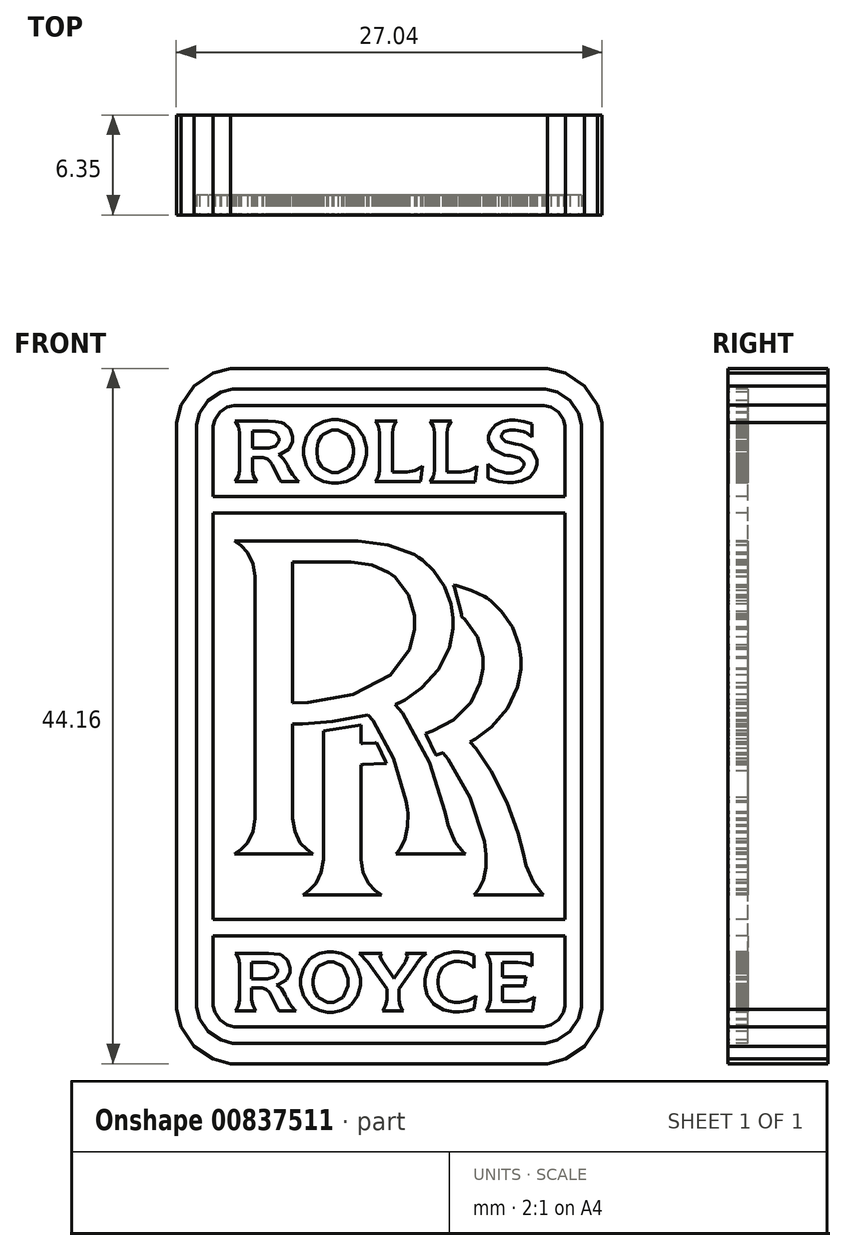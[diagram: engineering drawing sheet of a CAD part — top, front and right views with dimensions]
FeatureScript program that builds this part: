
annotation { "Feature Type Name" : "Feature", "Feature Type Description" : "" }
export const myFeature = defineFeature(function(context is Context, id is Id, definition is map)
    precondition{}
    {
        {
            var Q0;
            Q0=qCreatedBy(makeId("Front.planeOp"),FACE);
            var sketch = newSketch(context, id + "F0", { "sketchPlane" : qUnion([Q0])});
            skLineSegment(sketch, "E0", {"start": v(13.52, 18.27) * mm, "end": v(13.52, 18.64) * mm});
            skLineSegment(sketch, "E1", {"start": v(13.52, 18.64) * mm, "end": v(13.22, 19.75) * mm});
            skLineSegment(sketch, "E2", {"start": v(13.22, 19.75) * mm, "end": v(12.4, 20.97) * mm});
            skLineSegment(sketch, "E3", {"start": v(12.4, 20.97) * mm, "end": v(11.19, 21.79) * mm});
            skLineSegment(sketch, "E4", {"start": v(11.19, 21.79) * mm, "end": v(10.07, 22.08) * mm});
            skLineSegment(sketch, "E5", {"start": v(10.07, 22.08) * mm, "end": v(9.7, 22.08) * mm});
            skLineSegment(sketch, "E6", {"start": v(9.7, 22.08) * mm, "end": v(-9.7, 22.08) * mm});
            skLineSegment(sketch, "E7", {"start": v(-9.7, 22.08) * mm, "end": v(-10.07, 22.08) * mm});
            skLineSegment(sketch, "E8", {"start": v(-10.07, 22.08) * mm, "end": v(-11.19, 21.79) * mm});
            skLineSegment(sketch, "E9", {"start": v(-11.19, 21.79) * mm, "end": v(-12.4, 20.97) * mm});
            skLineSegment(sketch, "E10", {"start": v(-12.4, 20.97) * mm, "end": v(-13.22, 19.75) * mm});
            skLineSegment(sketch, "E11", {"start": v(-13.22, 19.75) * mm, "end": v(-13.52, 18.64) * mm});
            skLineSegment(sketch, "E12", {"start": v(-13.52, 18.64) * mm, "end": v(-13.52, 18.27) * mm});
            skLineSegment(sketch, "E13", {"start": v(-13.52, 18.27) * mm, "end": v(-13.52, -18.26) * mm});
            skLineSegment(sketch, "E14", {"start": v(-13.52, -18.26) * mm, "end": v(-13.52, -18.64) * mm});
            skLineSegment(sketch, "E15", {"start": v(-13.52, -18.64) * mm, "end": v(-13.22, -19.75) * mm});
            skLineSegment(sketch, "E16", {"start": v(-13.22, -19.75) * mm, "end": v(-12.4, -20.97) * mm});
            skLineSegment(sketch, "E17", {"start": v(-12.4, -20.97) * mm, "end": v(-11.19, -21.78) * mm});
            skLineSegment(sketch, "E18", {"start": v(-11.19, -21.78) * mm, "end": v(-10.07, -22.08) * mm});
            skLineSegment(sketch, "E19", {"start": v(-10.07, -22.08) * mm, "end": v(-9.7, -22.08) * mm});
            skLineSegment(sketch, "E20", {"start": v(-9.7, -22.08) * mm, "end": v(9.7, -22.08) * mm});
            skLineSegment(sketch, "E21", {"start": v(9.7, -22.08) * mm, "end": v(10.07, -22.08) * mm});
            skLineSegment(sketch, "E22", {"start": v(10.07, -22.08) * mm, "end": v(11.19, -21.78) * mm});
            skLineSegment(sketch, "E23", {"start": v(11.19, -21.78) * mm, "end": v(12.4, -20.97) * mm});
            skLineSegment(sketch, "E24", {"start": v(12.4, -20.97) * mm, "end": v(13.22, -19.75) * mm});
            skLineSegment(sketch, "E25", {"start": v(13.22, -19.75) * mm, "end": v(13.52, -18.64) * mm});
            skLineSegment(sketch, "E26", {"start": v(13.52, -18.64) * mm, "end": v(13.52, -18.26) * mm});
            skLineSegment(sketch, "E27", {"start": v(13.52, -18.26) * mm, "end": v(13.52, 18.27) * mm});
            skSolve(sketch);
        }
        {
            var Q0;
            Q0 = qSketchRegion(id + "F0", true);
            extrude(context, id + "F1", {"entities" : qUnion([Q0]), "depth" : 6.35 * mm, "offsetDistance" : 25.4 * mm});
        }
        {
            var Q0;
            Q0=makeQuery(id+"F1.opExtrude","CAP_FACE",FACE,{"disambiguationData":[OSD([sQuery(id+"F0.wireOp",EDGE,"E0"),sQuery(id+"F0.wireOp",EDGE,"E1"),sQuery(id+"F0.wireOp",EDGE,"E2"),sQuery(id+"F0.wireOp",EDGE,"E3"),sQuery(id+"F0.wireOp",EDGE,"E4"),sQuery(id+"F0.wireOp",EDGE,"E5"),sQuery(id+"F0.wireOp",EDGE,"E6"),sQuery(id+"F0.wireOp",EDGE,"E7"),sQuery(id+"F0.wireOp",EDGE,"E8"),sQuery(id+"F0.wireOp",EDGE,"E9"),sQuery(id+"F0.wireOp",EDGE,"E10"),sQuery(id+"F0.wireOp",EDGE,"E11"),sQuery(id+"F0.wireOp",EDGE,"E12"),sQuery(id+"F0.wireOp",EDGE,"E13"),sQuery(id+"F0.wireOp",EDGE,"E14"),sQuery(id+"F0.wireOp",EDGE,"E15"),sQuery(id+"F0.wireOp",EDGE,"E16"),sQuery(id+"F0.wireOp",EDGE,"E17"),sQuery(id+"F0.wireOp",EDGE,"E18"),sQuery(id+"F0.wireOp",EDGE,"E19"),sQuery(id+"F0.wireOp",EDGE,"E20"),sQuery(id+"F0.wireOp",EDGE,"E21"),sQuery(id+"F0.wireOp",EDGE,"E22"),sQuery(id+"F0.wireOp",EDGE,"E23"),sQuery(id+"F0.wireOp",EDGE,"E24"),sQuery(id+"F0.wireOp",EDGE,"E25"),sQuery(id+"F0.wireOp",EDGE,"E26"),sQuery(id+"F0.wireOp",EDGE,"E27")])],"isStart":false});
            var sketch = newSketch(context, id + "F2", { "sketchPlane" : qUnion([Q0])});
            skLineSegment(sketch, "E28", {"start": v(-12.23, 18.27) * mm, "end": v(-12.23, 18.51) * mm});
            skLineSegment(sketch, "E29", {"start": v(-12.23, 18.51) * mm, "end": v(-12.03, 19.24) * mm});
            skLineSegment(sketch, "E30", {"start": v(-12.03, 19.24) * mm, "end": v(-11.49, 20.04) * mm});
            skLineSegment(sketch, "E31", {"start": v(-11.49, 20.04) * mm, "end": v(-10.69, 20.58) * mm});
            skLineSegment(sketch, "E32", {"start": v(-10.69, 20.58) * mm, "end": v(-9.95, 20.78) * mm});
            skLineSegment(sketch, "E33", {"start": v(-9.95, 20.78) * mm, "end": v(-9.7, 20.78) * mm});
            skLineSegment(sketch, "E34", {"start": v(-9.7, 20.78) * mm, "end": v(9.69, 20.78) * mm});
            skLineSegment(sketch, "E35", {"start": v(9.69, 20.78) * mm, "end": v(9.93, 20.78) * mm});
            skLineSegment(sketch, "E36", {"start": v(9.93, 20.78) * mm, "end": v(10.68, 20.58) * mm});
            skLineSegment(sketch, "E37", {"start": v(10.68, 20.58) * mm, "end": v(11.48, 20.04) * mm});
            skLineSegment(sketch, "E38", {"start": v(11.48, 20.04) * mm, "end": v(12.03, 19.24) * mm});
            skLineSegment(sketch, "E39", {"start": v(12.03, 19.24) * mm, "end": v(12.23, 18.51) * mm});
            skLineSegment(sketch, "E40", {"start": v(12.23, 18.51) * mm, "end": v(12.23, 18.27) * mm});
            skLineSegment(sketch, "E41", {"start": v(12.23, 18.27) * mm, "end": v(12.23, -18.26) * mm});
            skLineSegment(sketch, "E42", {"start": v(12.23, -18.26) * mm, "end": v(12.23, -18.5) * mm});
            skLineSegment(sketch, "E43", {"start": v(12.23, -18.5) * mm, "end": v(12.03, -19.24) * mm});
            skLineSegment(sketch, "E44", {"start": v(12.03, -19.24) * mm, "end": v(11.48, -20.04) * mm});
            skLineSegment(sketch, "E45", {"start": v(11.48, -20.04) * mm, "end": v(10.68, -20.58) * mm});
            skLineSegment(sketch, "E46", {"start": v(10.68, -20.58) * mm, "end": v(9.93, -20.78) * mm});
            skLineSegment(sketch, "E47", {"start": v(9.93, -20.78) * mm, "end": v(9.69, -20.78) * mm});
            skLineSegment(sketch, "E48", {"start": v(9.69, -20.78) * mm, "end": v(-9.7, -20.78) * mm});
            skLineSegment(sketch, "E49", {"start": v(-9.7, -20.78) * mm, "end": v(-9.95, -20.78) * mm});
            skLineSegment(sketch, "E50", {"start": v(-9.95, -20.78) * mm, "end": v(-10.69, -20.58) * mm});
            skLineSegment(sketch, "E51", {"start": v(-10.69, -20.58) * mm, "end": v(-11.49, -20.04) * mm});
            skLineSegment(sketch, "E52", {"start": v(-11.49, -20.04) * mm, "end": v(-12.03, -19.24) * mm});
            skLineSegment(sketch, "E53", {"start": v(-12.03, -19.24) * mm, "end": v(-12.23, -18.5) * mm});
            skLineSegment(sketch, "E54", {"start": v(-12.23, -18.5) * mm, "end": v(-12.23, -18.26) * mm});
            skLineSegment(sketch, "E55", {"start": v(-12.23, -18.26) * mm, "end": v(-12.23, 18.27) * mm});
            skLineSegment(sketch, "E56", {"start": v(-11.18, 13.96) * mm, "end": v(-11.18, 18.27) * mm});
            skLineSegment(sketch, "E57", {"start": v(-11.18, 18.27) * mm, "end": v(-11.18, 18.4) * mm});
            skLineSegment(sketch, "E58", {"start": v(-11.18, 18.4) * mm, "end": v(-11.06, 18.84) * mm});
            skLineSegment(sketch, "E59", {"start": v(-11.06, 18.84) * mm, "end": v(-10.75, 19.3) * mm});
            skLineSegment(sketch, "E60", {"start": v(-10.75, 19.3) * mm, "end": v(-10.28, 19.62) * mm});
            skLineSegment(sketch, "E61", {"start": v(-10.28, 19.62) * mm, "end": v(-9.85, 19.74) * mm});
            skLineSegment(sketch, "E62", {"start": v(-9.85, 19.74) * mm, "end": v(-9.7, 19.74) * mm});
            skLineSegment(sketch, "E63", {"start": v(-9.7, 19.74) * mm, "end": v(9.69, 19.74) * mm});
            skLineSegment(sketch, "E64", {"start": v(9.69, 19.74) * mm, "end": v(9.83, 19.74) * mm});
            skLineSegment(sketch, "E65", {"start": v(9.83, 19.74) * mm, "end": v(10.27, 19.62) * mm});
            skLineSegment(sketch, "E66", {"start": v(10.27, 19.62) * mm, "end": v(10.75, 19.3) * mm});
            skLineSegment(sketch, "E67", {"start": v(10.75, 19.3) * mm, "end": v(11.06, 18.84) * mm});
            skLineSegment(sketch, "E68", {"start": v(11.06, 18.84) * mm, "end": v(11.18, 18.4) * mm});
            skLineSegment(sketch, "E69", {"start": v(11.18, 18.4) * mm, "end": v(11.18, 18.27) * mm});
            skLineSegment(sketch, "E70", {"start": v(11.18, 18.27) * mm, "end": v(11.18, 13.96) * mm});
            skLineSegment(sketch, "E71", {"start": v(11.18, 13.96) * mm, "end": v(-11.18, 13.96) * mm});
            skLineSegment(sketch, "E72", {"start": v(-11.18, 12.9) * mm, "end": v(11.18, 12.9) * mm});
            skLineSegment(sketch, "E73", {"start": v(11.18, 12.9) * mm, "end": v(11.18, -12.9) * mm});
            skLineSegment(sketch, "E74", {"start": v(11.18, -12.9) * mm, "end": v(-11.18, -12.9) * mm});
            skLineSegment(sketch, "E75", {"start": v(-11.18, -12.9) * mm, "end": v(-11.18, 12.9) * mm});
            skLineSegment(sketch, "E76", {"start": v(6.47, 16.07) * mm, "end": v(6.49, 16.03) * mm});
            skLineSegment(sketch, "E77", {"start": v(6.49, 16.03) * mm, "end": v(6.84, 15.74) * mm});
            skLineSegment(sketch, "E78", {"start": v(6.84, 15.74) * mm, "end": v(6.87, 15.73) * mm});
            skLineSegment(sketch, "E79", {"start": v(6.87, 15.73) * mm, "end": v(6.96, 15.68) * mm});
            skLineSegment(sketch, "E80", {"start": v(6.96, 15.68) * mm, "end": v(7.66, 15.47) * mm});
            skLineSegment(sketch, "E81", {"start": v(7.66, 15.47) * mm, "end": v(7.9, 15.47) * mm});
            skLineSegment(sketch, "E82", {"start": v(7.9, 15.47) * mm, "end": v(8.05, 15.47) * mm});
            skLineSegment(sketch, "E83", {"start": v(8.05, 15.47) * mm, "end": v(8.52, 15.63) * mm});
            skLineSegment(sketch, "E84", {"start": v(8.52, 15.63) * mm, "end": v(8.75, 15.94) * mm});
            skLineSegment(sketch, "E85", {"start": v(8.75, 15.94) * mm, "end": v(8.75, 16.05) * mm});
            skLineSegment(sketch, "E86", {"start": v(8.75, 16.05) * mm, "end": v(8.75, 16.15) * mm});
            skLineSegment(sketch, "E87", {"start": v(8.75, 16.15) * mm, "end": v(8.47, 16.44) * mm});
            skLineSegment(sketch, "E88", {"start": v(8.47, 16.44) * mm, "end": v(7.88, 16.58) * mm});
            skLineSegment(sketch, "E89", {"start": v(7.88, 16.58) * mm, "end": v(7.72, 16.6) * mm});
            skLineSegment(sketch, "E90", {"start": v(7.72, 16.6) * mm, "end": v(7.53, 16.63) * mm});
            skLineSegment(sketch, "E91", {"start": v(7.53, 16.63) * mm, "end": v(6.82, 16.96) * mm});
            skLineSegment(sketch, "E92", {"start": v(6.82, 16.96) * mm, "end": v(6.5, 17.52) * mm});
            skLineSegment(sketch, "E93", {"start": v(6.5, 17.52) * mm, "end": v(6.5, 17.71) * mm});
            skLineSegment(sketch, "E94", {"start": v(6.5, 17.71) * mm, "end": v(6.51, 17.82) * mm});
            skLineSegment(sketch, "E95", {"start": v(6.51, 17.82) * mm, "end": v(6.63, 18.16) * mm});
            skLineSegment(sketch, "E96", {"start": v(6.63, 18.16) * mm, "end": v(6.93, 18.52) * mm});
            skLineSegment(sketch, "E97", {"start": v(6.93, 18.52) * mm, "end": v(7.4, 18.76) * mm});
            skLineSegment(sketch, "E98", {"start": v(7.4, 18.76) * mm, "end": v(7.85, 18.84) * mm});
            skLineSegment(sketch, "E99", {"start": v(7.85, 18.84) * mm, "end": v(8, 18.84) * mm});
            skLineSegment(sketch, "E100", {"start": v(8, 18.84) * mm, "end": v(8.2, 18.84) * mm});
            skLineSegment(sketch, "E101", {"start": v(8.2, 18.84) * mm, "end": v(8.76, 18.76) * mm});
            skLineSegment(sketch, "E102", {"start": v(8.76, 18.76) * mm, "end": v(9.2, 18.62) * mm});
            skLineSegment(sketch, "E103", {"start": v(9.2, 18.62) * mm, "end": v(9.26, 18.59) * mm});
            skLineSegment(sketch, "E104", {"start": v(9.26, 18.59) * mm, "end": v(9.26, 17.75) * mm});
            skLineSegment(sketch, "E105", {"start": v(9.26, 17.75) * mm, "end": v(9.24, 17.8) * mm});
            skLineSegment(sketch, "E106", {"start": v(9.24, 17.8) * mm, "end": v(8.84, 18.07) * mm});
            skLineSegment(sketch, "E107", {"start": v(8.84, 18.07) * mm, "end": v(8.8, 18.1) * mm});
            skLineSegment(sketch, "E108", {"start": v(8.8, 18.1) * mm, "end": v(8.73, 18.12) * mm});
            skLineSegment(sketch, "E109", {"start": v(8.73, 18.12) * mm, "end": v(8.18, 18.22) * mm});
            skLineSegment(sketch, "E110", {"start": v(8.18, 18.22) * mm, "end": v(8, 18.22) * mm});
            skLineSegment(sketch, "E111", {"start": v(8, 18.22) * mm, "end": v(7.88, 18.22) * mm});
            skLineSegment(sketch, "E112", {"start": v(7.88, 18.22) * mm, "end": v(7.5, 18.11) * mm});
            skLineSegment(sketch, "E113", {"start": v(7.5, 18.11) * mm, "end": v(7.32, 17.9) * mm});
            skLineSegment(sketch, "E114", {"start": v(7.32, 17.9) * mm, "end": v(7.32, 17.84) * mm});
            skLineSegment(sketch, "E115", {"start": v(7.32, 17.84) * mm, "end": v(7.32, 17.75) * mm});
            skLineSegment(sketch, "E116", {"start": v(7.32, 17.75) * mm, "end": v(7.58, 17.48) * mm});
            skLineSegment(sketch, "E117", {"start": v(7.58, 17.48) * mm, "end": v(8.22, 17.32) * mm});
            skLineSegment(sketch, "E118", {"start": v(8.22, 17.32) * mm, "end": v(8.4, 17.28) * mm});
            skLineSegment(sketch, "E119", {"start": v(8.4, 17.28) * mm, "end": v(8.6, 17.25) * mm});
            skLineSegment(sketch, "E120", {"start": v(8.6, 17.25) * mm, "end": v(9.28, 16.91) * mm});
            skLineSegment(sketch, "E121", {"start": v(9.28, 16.91) * mm, "end": v(9.58, 16.32) * mm});
            skLineSegment(sketch, "E122", {"start": v(9.58, 16.32) * mm, "end": v(9.58, 16.15) * mm});
            skLineSegment(sketch, "E123", {"start": v(9.58, 16.15) * mm, "end": v(9.58, 16.02) * mm});
            skLineSegment(sketch, "E124", {"start": v(9.58, 16.02) * mm, "end": v(9.46, 15.63) * mm});
            skLineSegment(sketch, "E125", {"start": v(9.46, 15.63) * mm, "end": v(9.13, 15.22) * mm});
            skLineSegment(sketch, "E126", {"start": v(9.13, 15.22) * mm, "end": v(8.6, 14.96) * mm});
            skLineSegment(sketch, "E127", {"start": v(8.6, 14.96) * mm, "end": v(8.07, 14.87) * mm});
            skLineSegment(sketch, "E128", {"start": v(8.07, 14.87) * mm, "end": v(7.9, 14.87) * mm});
            skLineSegment(sketch, "E129", {"start": v(7.9, 14.87) * mm, "end": v(7.7, 14.87) * mm});
            skLineSegment(sketch, "E130", {"start": v(7.7, 14.87) * mm, "end": v(7.14, 14.94) * mm});
            skLineSegment(sketch, "E131", {"start": v(7.14, 14.94) * mm, "end": v(6.55, 15.1) * mm});
            skLineSegment(sketch, "E132", {"start": v(6.55, 15.1) * mm, "end": v(6.47, 15.15) * mm});
            skLineSegment(sketch, "E133", {"start": v(6.47, 15.15) * mm, "end": v(6.47, 16.07) * mm});
            skLineSegment(sketch, "E134", {"start": v(-6.23, 15.9) * mm, "end": v(-6.28, 15.99) * mm});
            skLineSegment(sketch, "E135", {"start": v(-6.28, 15.99) * mm, "end": v(-6.5, 16.37) * mm});
            skLineSegment(sketch, "E136", {"start": v(-6.5, 16.37) * mm, "end": v(-6.78, 16.63) * mm});
            skLineSegment(sketch, "E137", {"start": v(-6.78, 16.63) * mm, "end": v(-6.85, 16.66) * mm});
            skLineSegment(sketch, "E138", {"start": v(-6.85, 16.66) * mm, "end": v(-6.7, 16.7) * mm});
            skLineSegment(sketch, "E139", {"start": v(-6.7, 16.7) * mm, "end": v(-6.18, 17.01) * mm});
            skLineSegment(sketch, "E140", {"start": v(-6.18, 17.01) * mm, "end": v(-5.95, 17.49) * mm});
            skLineSegment(sketch, "E141", {"start": v(-5.95, 17.49) * mm, "end": v(-5.95, 17.65) * mm});
            skLineSegment(sketch, "E142", {"start": v(-5.95, 17.65) * mm, "end": v(-5.95, 17.8) * mm});
            skLineSegment(sketch, "E143", {"start": v(-5.95, 17.8) * mm, "end": v(-6.11, 18.29) * mm});
            skLineSegment(sketch, "E144", {"start": v(-6.11, 18.29) * mm, "end": v(-6.47, 18.63) * mm});
            skLineSegment(sketch, "E145", {"start": v(-6.47, 18.63) * mm, "end": v(-6.57, 18.67) * mm});
            skLineSegment(sketch, "E146", {"start": v(-6.57, 18.67) * mm, "end": v(-6.64, 18.7) * mm});
            skLineSegment(sketch, "E147", {"start": v(-6.64, 18.7) * mm, "end": v(-7.02, 18.76) * mm});
            skLineSegment(sketch, "E148", {"start": v(-7.02, 18.76) * mm, "end": v(-7.48, 18.78) * mm});
            skLineSegment(sketch, "E149", {"start": v(-7.48, 18.78) * mm, "end": v(-7.64, 18.78) * mm});
            skLineSegment(sketch, "E150", {"start": v(-7.64, 18.78) * mm, "end": v(-9.6, 18.78) * mm});
            skLineSegment(sketch, "E151", {"start": v(-9.6, 18.78) * mm, "end": v(-9.55, 18.75) * mm});
            skLineSegment(sketch, "E152", {"start": v(-9.55, 18.75) * mm, "end": v(-9.38, 18.43) * mm});
            skLineSegment(sketch, "E153", {"start": v(-9.38, 18.43) * mm, "end": v(-9.3, 18.05) * mm});
            skLineSegment(sketch, "E154", {"start": v(-9.3, 18.05) * mm, "end": v(-9.3, 17.92) * mm});
            skLineSegment(sketch, "E155", {"start": v(-9.3, 17.92) * mm, "end": v(-9.3, 15.77) * mm});
            skLineSegment(sketch, "E156", {"start": v(-9.3, 15.77) * mm, "end": v(-9.3, 15.64) * mm});
            skLineSegment(sketch, "E157", {"start": v(-9.3, 15.64) * mm, "end": v(-9.38, 15.27) * mm});
            skLineSegment(sketch, "E158", {"start": v(-9.38, 15.27) * mm, "end": v(-9.55, 14.96) * mm});
            skLineSegment(sketch, "E159", {"start": v(-9.55, 14.96) * mm, "end": v(-9.6, 14.94) * mm});
            skLineSegment(sketch, "E160", {"start": v(-9.6, 14.94) * mm, "end": v(-8.2, 14.94) * mm});
            skLineSegment(sketch, "E161", {"start": v(-8.2, 14.94) * mm, "end": v(-8.24, 14.96) * mm});
            skLineSegment(sketch, "E162", {"start": v(-8.24, 14.96) * mm, "end": v(-8.41, 15.27) * mm});
            skLineSegment(sketch, "E163", {"start": v(-8.41, 15.27) * mm, "end": v(-8.5, 15.64) * mm});
            skLineSegment(sketch, "E164", {"start": v(-8.5, 15.64) * mm, "end": v(-8.5, 15.77) * mm});
            skLineSegment(sketch, "E165", {"start": v(-8.5, 15.77) * mm, "end": v(-8.5, 16.45) * mm});
            skLineSegment(sketch, "E166", {"start": v(-8.5, 16.45) * mm, "end": v(-7.9, 16.45) * mm});
            skLineSegment(sketch, "E167", {"start": v(-7.9, 16.45) * mm, "end": v(-7.8, 16.45) * mm});
            skLineSegment(sketch, "E168", {"start": v(-7.8, 16.45) * mm, "end": v(-7.53, 16.37) * mm});
            skLineSegment(sketch, "E169", {"start": v(-7.53, 16.37) * mm, "end": v(-7.33, 16.17) * mm});
            skLineSegment(sketch, "E170", {"start": v(-7.33, 16.17) * mm, "end": v(-7.3, 16.11) * mm});
            skLineSegment(sketch, "E171", {"start": v(-7.3, 16.11) * mm, "end": v(-7.24, 16.03) * mm});
            skLineSegment(sketch, "E172", {"start": v(-7.24, 16.03) * mm, "end": v(-6.74, 15.03) * mm});
            skLineSegment(sketch, "E173", {"start": v(-6.74, 15.03) * mm, "end": v(-6.68, 14.94) * mm});
            skLineSegment(sketch, "E174", {"start": v(-6.68, 14.94) * mm, "end": v(-5.55, 14.94) * mm});
            skLineSegment(sketch, "E175", {"start": v(-5.55, 14.94) * mm, "end": v(-5.63, 15) * mm});
            skLineSegment(sketch, "E176", {"start": v(-5.63, 15) * mm, "end": v(-5.95, 15.37) * mm});
            skLineSegment(sketch, "E177", {"start": v(-5.95, 15.37) * mm, "end": v(-6.19, 15.8) * mm});
            skLineSegment(sketch, "E178", {"start": v(-6.19, 15.8) * mm, "end": v(-6.23, 15.9) * mm});
            skLineSegment(sketch, "E179", {"start": v(-6.78, 17.6) * mm, "end": v(-6.78, 17.5) * mm});
            skLineSegment(sketch, "E180", {"start": v(-6.78, 17.5) * mm, "end": v(-7, 17.2) * mm});
            skLineSegment(sketch, "E181", {"start": v(-7, 17.2) * mm, "end": v(-7.45, 17.07) * mm});
            skLineSegment(sketch, "E182", {"start": v(-7.45, 17.07) * mm, "end": v(-7.6, 17.07) * mm});
            skLineSegment(sketch, "E183", {"start": v(-7.6, 17.07) * mm, "end": v(-8.5, 17.07) * mm});
            skLineSegment(sketch, "E184", {"start": v(-8.5, 17.07) * mm, "end": v(-8.5, 18.16) * mm});
            skLineSegment(sketch, "E185", {"start": v(-8.5, 18.16) * mm, "end": v(-7.6, 18.16) * mm});
            skLineSegment(sketch, "E186", {"start": v(-7.6, 18.16) * mm, "end": v(-7.45, 18.16) * mm});
            skLineSegment(sketch, "E187", {"start": v(-7.45, 18.16) * mm, "end": v(-7, 18.03) * mm});
            skLineSegment(sketch, "E188", {"start": v(-7, 18.03) * mm, "end": v(-6.78, 17.71) * mm});
            skLineSegment(sketch, "E189", {"start": v(-6.78, 17.71) * mm, "end": v(-6.78, 17.6) * mm});
            skLineSegment(sketch, "E190", {"start": v(-4.05, 15.83) * mm, "end": v(-4.11, 15.89) * mm});
            skLineSegment(sketch, "E191", {"start": v(-4.11, 15.89) * mm, "end": v(-4.31, 16.25) * mm});
            skLineSegment(sketch, "E192", {"start": v(-4.31, 16.25) * mm, "end": v(-4.4, 16.7) * mm});
            skLineSegment(sketch, "E193", {"start": v(-4.4, 16.7) * mm, "end": v(-4.4, 16.86) * mm});
            skLineSegment(sketch, "E194", {"start": v(-4.4, 16.86) * mm, "end": v(-4.4, 17) * mm});
            skLineSegment(sketch, "E195", {"start": v(-4.4, 17) * mm, "end": v(-4.31, 17.45) * mm});
            skLineSegment(sketch, "E196", {"start": v(-4.31, 17.45) * mm, "end": v(-4.11, 17.82) * mm});
            skLineSegment(sketch, "E197", {"start": v(-4.11, 17.82) * mm, "end": v(-4.05, 17.88) * mm});
            skLineSegment(sketch, "E198", {"start": v(-4.05, 17.88) * mm, "end": v(-4, 17.93) * mm});
            skLineSegment(sketch, "E199", {"start": v(-4, 17.93) * mm, "end": v(-3.43, 18.2) * mm});
            skLineSegment(sketch, "E200", {"start": v(-3.43, 18.2) * mm, "end": v(-3.24, 18.2) * mm});
            skLineSegment(sketch, "E201", {"start": v(-3.24, 18.2) * mm, "end": v(-3.04, 18.2) * mm});
            skLineSegment(sketch, "E202", {"start": v(-3.04, 18.2) * mm, "end": v(-2.48, 17.93) * mm});
            skLineSegment(sketch, "E203", {"start": v(-2.48, 17.93) * mm, "end": v(-2.43, 17.88) * mm});
            skLineSegment(sketch, "E204", {"start": v(-2.43, 17.88) * mm, "end": v(-2.38, 17.82) * mm});
            skLineSegment(sketch, "E205", {"start": v(-2.38, 17.82) * mm, "end": v(-2.16, 17.45) * mm});
            skLineSegment(sketch, "E206", {"start": v(-2.16, 17.45) * mm, "end": v(-2.07, 17) * mm});
            skLineSegment(sketch, "E207", {"start": v(-2.07, 17) * mm, "end": v(-2.07, 16.86) * mm});
            skLineSegment(sketch, "E208", {"start": v(-2.07, 16.86) * mm, "end": v(-2.07, 16.7) * mm});
            skLineSegment(sketch, "E209", {"start": v(-2.07, 16.7) * mm, "end": v(-2.16, 16.25) * mm});
            skLineSegment(sketch, "E210", {"start": v(-2.16, 16.25) * mm, "end": v(-2.38, 15.89) * mm});
            skLineSegment(sketch, "E211", {"start": v(-2.38, 15.89) * mm, "end": v(-2.43, 15.83) * mm});
            skLineSegment(sketch, "E212", {"start": v(-2.43, 15.83) * mm, "end": v(-2.48, 15.78) * mm});
            skLineSegment(sketch, "E213", {"start": v(-2.48, 15.78) * mm, "end": v(-3.05, 15.51) * mm});
            skLineSegment(sketch, "E214", {"start": v(-3.05, 15.51) * mm, "end": v(-3.24, 15.51) * mm});
            skLineSegment(sketch, "E215", {"start": v(-3.24, 15.51) * mm, "end": v(-3.45, 15.51) * mm});
            skLineSegment(sketch, "E216", {"start": v(-3.45, 15.51) * mm, "end": v(-4, 15.78) * mm});
            skLineSegment(sketch, "E217", {"start": v(-4, 15.78) * mm, "end": v(-4.05, 15.83) * mm});
            skLineSegment(sketch, "E218", {"start": v(-3.24, 14.83) * mm, "end": v(-3.06, 14.83) * mm});
            skLineSegment(sketch, "E219", {"start": v(-3.06, 14.83) * mm, "end": v(-2.51, 14.94) * mm});
            skLineSegment(sketch, "E220", {"start": v(-2.51, 14.94) * mm, "end": v(-2, 15.2) * mm});
            skLineSegment(sketch, "E221", {"start": v(-2, 15.2) * mm, "end": v(-1.92, 15.28) * mm});
            skLineSegment(sketch, "E222", {"start": v(-1.92, 15.28) * mm, "end": v(-1.82, 15.36) * mm});
            skLineSegment(sketch, "E223", {"start": v(-1.82, 15.36) * mm, "end": v(-1.43, 15.92) * mm});
            skLineSegment(sketch, "E224", {"start": v(-1.43, 15.92) * mm, "end": v(-1.24, 16.62) * mm});
            skLineSegment(sketch, "E225", {"start": v(-1.24, 16.62) * mm, "end": v(-1.24, 16.86) * mm});
            skLineSegment(sketch, "E226", {"start": v(-1.24, 16.86) * mm, "end": v(-1.24, 17.09) * mm});
            skLineSegment(sketch, "E227", {"start": v(-1.24, 17.09) * mm, "end": v(-1.43, 17.78) * mm});
            skLineSegment(sketch, "E228", {"start": v(-1.43, 17.78) * mm, "end": v(-1.82, 18.35) * mm});
            skLineSegment(sketch, "E229", {"start": v(-1.82, 18.35) * mm, "end": v(-1.92, 18.44) * mm});
            skLineSegment(sketch, "E230", {"start": v(-1.92, 18.44) * mm, "end": v(-2, 18.5) * mm});
            skLineSegment(sketch, "E231", {"start": v(-2, 18.5) * mm, "end": v(-2.51, 18.75) * mm});
            skLineSegment(sketch, "E232", {"start": v(-2.51, 18.75) * mm, "end": v(-3.06, 18.86) * mm});
            skLineSegment(sketch, "E233", {"start": v(-3.06, 18.86) * mm, "end": v(-3.24, 18.86) * mm});
            skLineSegment(sketch, "E234", {"start": v(-3.24, 18.86) * mm, "end": v(-3.43, 18.86) * mm});
            skLineSegment(sketch, "E235", {"start": v(-3.43, 18.86) * mm, "end": v(-3.98, 18.75) * mm});
            skLineSegment(sketch, "E236", {"start": v(-3.98, 18.75) * mm, "end": v(-4.48, 18.5) * mm});
            skLineSegment(sketch, "E237", {"start": v(-4.48, 18.5) * mm, "end": v(-4.57, 18.44) * mm});
            skLineSegment(sketch, "E238", {"start": v(-4.57, 18.44) * mm, "end": v(-4.67, 18.35) * mm});
            skLineSegment(sketch, "E239", {"start": v(-4.67, 18.35) * mm, "end": v(-5.06, 17.78) * mm});
            skLineSegment(sketch, "E240", {"start": v(-5.06, 17.78) * mm, "end": v(-5.25, 17.09) * mm});
            skLineSegment(sketch, "E241", {"start": v(-5.25, 17.09) * mm, "end": v(-5.25, 16.86) * mm});
            skLineSegment(sketch, "E242", {"start": v(-5.25, 16.86) * mm, "end": v(-5.25, 16.62) * mm});
            skLineSegment(sketch, "E243", {"start": v(-5.25, 16.62) * mm, "end": v(-5.06, 15.92) * mm});
            skLineSegment(sketch, "E244", {"start": v(-5.06, 15.92) * mm, "end": v(-4.67, 15.36) * mm});
            skLineSegment(sketch, "E245", {"start": v(-4.67, 15.36) * mm, "end": v(-4.57, 15.28) * mm});
            skLineSegment(sketch, "E246", {"start": v(-4.57, 15.28) * mm, "end": v(-4.48, 15.2) * mm});
            skLineSegment(sketch, "E247", {"start": v(-4.48, 15.2) * mm, "end": v(-3.97, 14.94) * mm});
            skLineSegment(sketch, "E248", {"start": v(-3.97, 14.94) * mm, "end": v(-3.43, 14.83) * mm});
            skLineSegment(sketch, "E249", {"start": v(-3.43, 14.83) * mm, "end": v(-3.24, 14.83) * mm});
            skLineSegment(sketch, "E250", {"start": v(2.3, 15.92) * mm, "end": v(2.25, 15.85) * mm});
            skLineSegment(sketch, "E251", {"start": v(2.25, 15.85) * mm, "end": v(1.83, 15.63) * mm});
            skLineSegment(sketch, "E252", {"start": v(1.83, 15.63) * mm, "end": v(1.32, 15.56) * mm});
            skLineSegment(sketch, "E253", {"start": v(1.32, 15.56) * mm, "end": v(1.15, 15.56) * mm});
            skLineSegment(sketch, "E254", {"start": v(1.15, 15.56) * mm, "end": v(0.4, 15.56) * mm});
            skLineSegment(sketch, "E255", {"start": v(0.4, 15.56) * mm, "end": v(0.4, 17.92) * mm});
            skLineSegment(sketch, "E256", {"start": v(0.4, 17.92) * mm, "end": v(0.4, 18.05) * mm});
            skLineSegment(sketch, "E257", {"start": v(0.4, 18.05) * mm, "end": v(0.48, 18.42) * mm});
            skLineSegment(sketch, "E258", {"start": v(0.48, 18.42) * mm, "end": v(0.64, 18.75) * mm});
            skLineSegment(sketch, "E259", {"start": v(0.64, 18.75) * mm, "end": v(0.68, 18.78) * mm});
            skLineSegment(sketch, "E260", {"start": v(0.68, 18.78) * mm, "end": v(-0.7, 18.78) * mm});
            skLineSegment(sketch, "E261", {"start": v(-0.7, 18.78) * mm, "end": v(-0.66, 18.75) * mm});
            skLineSegment(sketch, "E262", {"start": v(-0.66, 18.75) * mm, "end": v(-0.48, 18.42) * mm});
            skLineSegment(sketch, "E263", {"start": v(-0.48, 18.42) * mm, "end": v(-0.4, 18.05) * mm});
            skLineSegment(sketch, "E264", {"start": v(-0.4, 18.05) * mm, "end": v(-0.4, 17.92) * mm});
            skLineSegment(sketch, "E265", {"start": v(-0.4, 17.92) * mm, "end": v(-0.4, 15.77) * mm});
            skLineSegment(sketch, "E266", {"start": v(-0.4, 15.77) * mm, "end": v(-0.4, 15.64) * mm});
            skLineSegment(sketch, "E267", {"start": v(-0.4, 15.64) * mm, "end": v(-0.48, 15.27) * mm});
            skLineSegment(sketch, "E268", {"start": v(-0.48, 15.27) * mm, "end": v(-0.66, 14.97) * mm});
            skLineSegment(sketch, "E269", {"start": v(-0.66, 14.97) * mm, "end": v(-0.7, 14.94) * mm});
            skLineSegment(sketch, "E270", {"start": v(-0.7, 14.94) * mm, "end": v(2.18, 14.94) * mm});
            skLineSegment(sketch, "E271", {"start": v(2.18, 14.94) * mm, "end": v(2.3, 15.92) * mm});
            skLineSegment(sketch, "E272", {"start": v(5.78, 15.92) * mm, "end": v(5.73, 15.85) * mm});
            skLineSegment(sketch, "E273", {"start": v(5.73, 15.85) * mm, "end": v(5.31, 15.63) * mm});
            skLineSegment(sketch, "E274", {"start": v(5.31, 15.63) * mm, "end": v(4.75, 15.55) * mm});
            skLineSegment(sketch, "E275", {"start": v(4.75, 15.55) * mm, "end": v(4.63, 15.56) * mm});
            skLineSegment(sketch, "E276", {"start": v(4.63, 15.56) * mm, "end": v(3.86, 15.56) * mm});
            skLineSegment(sketch, "E277", {"start": v(3.86, 15.56) * mm, "end": v(3.86, 17.92) * mm});
            skLineSegment(sketch, "E278", {"start": v(3.86, 17.92) * mm, "end": v(3.86, 18.05) * mm});
            skLineSegment(sketch, "E279", {"start": v(3.86, 18.05) * mm, "end": v(3.94, 18.42) * mm});
            skLineSegment(sketch, "E280", {"start": v(3.94, 18.42) * mm, "end": v(4.11, 18.75) * mm});
            skLineSegment(sketch, "E281", {"start": v(4.11, 18.75) * mm, "end": v(4.16, 18.78) * mm});
            skLineSegment(sketch, "E282", {"start": v(4.16, 18.78) * mm, "end": v(2.77, 18.78) * mm});
            skLineSegment(sketch, "E283", {"start": v(2.77, 18.78) * mm, "end": v(2.82, 18.75) * mm});
            skLineSegment(sketch, "E284", {"start": v(2.82, 18.75) * mm, "end": v(3, 18.42) * mm});
            skLineSegment(sketch, "E285", {"start": v(3, 18.42) * mm, "end": v(3.07, 18.05) * mm});
            skLineSegment(sketch, "E286", {"start": v(3.07, 18.05) * mm, "end": v(3.07, 17.92) * mm});
            skLineSegment(sketch, "E287", {"start": v(3.07, 17.92) * mm, "end": v(3.07, 15.77) * mm});
            skLineSegment(sketch, "E288", {"start": v(3.07, 15.77) * mm, "end": v(3.07, 15.64) * mm});
            skLineSegment(sketch, "E289", {"start": v(3.07, 15.64) * mm, "end": v(3, 15.26) * mm});
            skLineSegment(sketch, "E290", {"start": v(3, 15.26) * mm, "end": v(2.82, 14.95) * mm});
            skLineSegment(sketch, "E291", {"start": v(2.82, 14.95) * mm, "end": v(2.77, 14.91) * mm});
            skLineSegment(sketch, "E292", {"start": v(2.77, 14.91) * mm, "end": v(5.63, 14.91) * mm});
            skLineSegment(sketch, "E293", {"start": v(5.63, 14.91) * mm, "end": v(5.78, 15.92) * mm});
            skLineSegment(sketch, "E294", {"start": v(-11.18, -13.96) * mm, "end": v(-11.18, -18.26) * mm});
            skLineSegment(sketch, "E295", {"start": v(-11.18, -18.26) * mm, "end": v(-11.18, -18.4) * mm});
            skLineSegment(sketch, "E296", {"start": v(-11.18, -18.4) * mm, "end": v(-11.06, -18.84) * mm});
            skLineSegment(sketch, "E297", {"start": v(-11.06, -18.84) * mm, "end": v(-10.75, -19.3) * mm});
            skLineSegment(sketch, "E298", {"start": v(-10.75, -19.3) * mm, "end": v(-10.28, -19.62) * mm});
            skLineSegment(sketch, "E299", {"start": v(-10.28, -19.62) * mm, "end": v(-9.85, -19.74) * mm});
            skLineSegment(sketch, "E300", {"start": v(-9.85, -19.74) * mm, "end": v(-9.7, -19.74) * mm});
            skLineSegment(sketch, "E301", {"start": v(-9.7, -19.74) * mm, "end": v(9.69, -19.74) * mm});
            skLineSegment(sketch, "E302", {"start": v(9.69, -19.74) * mm, "end": v(9.83, -19.74) * mm});
            skLineSegment(sketch, "E303", {"start": v(9.83, -19.74) * mm, "end": v(10.27, -19.62) * mm});
            skLineSegment(sketch, "E304", {"start": v(10.27, -19.62) * mm, "end": v(10.75, -19.3) * mm});
            skLineSegment(sketch, "E305", {"start": v(10.75, -19.3) * mm, "end": v(11.06, -18.84) * mm});
            skLineSegment(sketch, "E306", {"start": v(11.06, -18.84) * mm, "end": v(11.18, -18.4) * mm});
            skLineSegment(sketch, "E307", {"start": v(11.18, -18.4) * mm, "end": v(11.18, -18.26) * mm});
            skLineSegment(sketch, "E308", {"start": v(11.18, -18.26) * mm, "end": v(11.18, -13.96) * mm});
            skLineSegment(sketch, "E309", {"start": v(11.18, -13.96) * mm, "end": v(-11.18, -13.96) * mm});
            skLineSegment(sketch, "E310", {"start": v(-1.6, -8.8) * mm, "end": v(-1.6, -3.05) * mm});
            skLineSegment(sketch, "E311", {"start": v(-1.6, -3.05) * mm, "end": v(-1.46, -3.05) * mm});
            skLineSegment(sketch, "E312", {"start": v(-1.46, -3.05) * mm, "end": v(-0.11, -2.98) * mm});
            skLineSegment(sketch, "E313", {"start": v(-0.11, -2.98) * mm, "end": v(0.02, -2.96) * mm});
            skLineSegment(sketch, "E314", {"start": v(0.02, -2.96) * mm, "end": v(-0.03, -2.85) * mm});
            skLineSegment(sketch, "E315", {"start": v(-0.03, -2.85) * mm, "end": v(-0.54, -1.75) * mm});
            skLineSegment(sketch, "E316", {"start": v(-0.54, -1.75) * mm, "end": v(-0.6, -1.64) * mm});
            skLineSegment(sketch, "E317", {"start": v(-0.6, -1.64) * mm, "end": v(-0.68, -1.65) * mm});
            skLineSegment(sketch, "E318", {"start": v(-0.68, -1.65) * mm, "end": v(-1.52, -1.7) * mm});
            skLineSegment(sketch, "E319", {"start": v(-1.52, -1.7) * mm, "end": v(-1.6, -1.7) * mm});
            skLineSegment(sketch, "E320", {"start": v(-1.6, -1.7) * mm, "end": v(-1.6, -0.51) * mm});
            skLineSegment(sketch, "E321", {"start": v(-1.6, -0.51) * mm, "end": v(-1.79, -0.56) * mm});
            skLineSegment(sketch, "E322", {"start": v(-1.79, -0.56) * mm, "end": v(-3.78, -0.87) * mm});
            skLineSegment(sketch, "E323", {"start": v(-3.78, -0.87) * mm, "end": v(-3.99, -0.9) * mm});
            skLineSegment(sketch, "E324", {"start": v(-3.99, -0.9) * mm, "end": v(-3.99, -8.8) * mm});
            skLineSegment(sketch, "E325", {"start": v(-3.99, -8.8) * mm, "end": v(-3.99, -9.06) * mm});
            skLineSegment(sketch, "E326", {"start": v(-3.99, -9.06) * mm, "end": v(-4.12, -9.88) * mm});
            skLineSegment(sketch, "E327", {"start": v(-4.12, -9.88) * mm, "end": v(-4.46, -10.6) * mm});
            skLineSegment(sketch, "E328", {"start": v(-4.46, -10.6) * mm, "end": v(-4.88, -11.04) * mm});
            skLineSegment(sketch, "E329", {"start": v(-4.88, -11.04) * mm, "end": v(-5.19, -11.26) * mm});
            skLineSegment(sketch, "E330", {"start": v(-5.19, -11.26) * mm, "end": v(-5.3, -11.33) * mm});
            skLineSegment(sketch, "E331", {"start": v(-5.3, -11.33) * mm, "end": v(-0.3, -11.33) * mm});
            skLineSegment(sketch, "E332", {"start": v(-0.3, -11.33) * mm, "end": v(-0.4, -11.26) * mm});
            skLineSegment(sketch, "E333", {"start": v(-0.4, -11.26) * mm, "end": v(-0.7, -11.04) * mm});
            skLineSegment(sketch, "E334", {"start": v(-0.7, -11.04) * mm, "end": v(-1.13, -10.6) * mm});
            skLineSegment(sketch, "E335", {"start": v(-1.13, -10.6) * mm, "end": v(-1.46, -9.88) * mm});
            skLineSegment(sketch, "E336", {"start": v(-1.46, -9.88) * mm, "end": v(-1.6, -9.06) * mm});
            skLineSegment(sketch, "E337", {"start": v(-1.6, -9.06) * mm, "end": v(-1.6, -8.8) * mm});
            skLineSegment(sketch, "E338", {"start": v(10, -11.3) * mm, "end": v(9.9, -11.21) * mm});
            skLineSegment(sketch, "E339", {"start": v(9.9, -11.21) * mm, "end": v(9.36, -10.53) * mm});
            skLineSegment(sketch, "E340", {"start": v(9.36, -10.53) * mm, "end": v(8.9, -9.45) * mm});
            skLineSegment(sketch, "E341", {"start": v(8.9, -9.45) * mm, "end": v(8.83, -9.15) * mm});
            skLineSegment(sketch, "E342", {"start": v(8.83, -9.15) * mm, "end": v(8.74, -8.7) * mm});
            skLineSegment(sketch, "E343", {"start": v(8.74, -8.7) * mm, "end": v(8.38, -7.39) * mm});
            skLineSegment(sketch, "E344", {"start": v(8.38, -7.39) * mm, "end": v(7.67, -5.43) * mm});
            skLineSegment(sketch, "E345", {"start": v(7.67, -5.43) * mm, "end": v(6.67, -3.45) * mm});
            skLineSegment(sketch, "E346", {"start": v(6.67, -3.45) * mm, "end": v(5.7, -2.02) * mm});
            skLineSegment(sketch, "E347", {"start": v(5.7, -2.02) * mm, "end": v(5.31, -1.6) * mm});
            skLineSegment(sketch, "E348", {"start": v(5.31, -1.6) * mm, "end": v(5.68, -1.4) * mm});
            skLineSegment(sketch, "E349", {"start": v(5.68, -1.4) * mm, "end": v(6.68, -0.65) * mm});
            skLineSegment(sketch, "E350", {"start": v(6.68, -0.65) * mm, "end": v(7.7, 0.52) * mm});
            skLineSegment(sketch, "E351", {"start": v(7.7, 0.52) * mm, "end": v(8.35, 1.88) * mm});
            skLineSegment(sketch, "E352", {"start": v(8.35, 1.88) * mm, "end": v(8.58, 3.03) * mm});
            skLineSegment(sketch, "E353", {"start": v(8.58, 3.03) * mm, "end": v(8.58, 3.41) * mm});
            skLineSegment(sketch, "E354", {"start": v(8.58, 3.41) * mm, "end": v(8.58, 3.7) * mm});
            skLineSegment(sketch, "E355", {"start": v(8.58, 3.7) * mm, "end": v(8.44, 4.57) * mm});
            skLineSegment(sketch, "E356", {"start": v(8.44, 4.57) * mm, "end": v(8.03, 5.69) * mm});
            skLineSegment(sketch, "E357", {"start": v(8.03, 5.69) * mm, "end": v(7.34, 6.7) * mm});
            skLineSegment(sketch, "E358", {"start": v(7.34, 6.7) * mm, "end": v(6.66, 7.36) * mm});
            skLineSegment(sketch, "E359", {"start": v(6.66, 7.36) * mm, "end": v(6.4, 7.53) * mm});
            skLineSegment(sketch, "E360", {"start": v(6.4, 7.53) * mm, "end": v(6.25, 7.63) * mm});
            skLineSegment(sketch, "E361", {"start": v(6.25, 7.63) * mm, "end": v(5.42, 8.03) * mm});
            skLineSegment(sketch, "E362", {"start": v(5.42, 8.03) * mm, "end": v(4.48, 8.32) * mm});
            skLineSegment(sketch, "E363", {"start": v(4.48, 8.32) * mm, "end": v(4.27, 8.36) * mm});
            skLineSegment(sketch, "E364", {"start": v(4.27, 8.36) * mm, "end": v(4.34, 8.2) * mm});
            skLineSegment(sketch, "E365", {"start": v(4.34, 8.2) * mm, "end": v(4.8, 6.53) * mm});
            skLineSegment(sketch, "E366", {"start": v(4.8, 6.53) * mm, "end": v(4.8, 6.36) * mm});
            skLineSegment(sketch, "E367", {"start": v(4.8, 6.36) * mm, "end": v(5.02, 6.19) * mm});
            skLineSegment(sketch, "E368", {"start": v(5.02, 6.19) * mm, "end": v(5.8, 5.08) * mm});
            skLineSegment(sketch, "E369", {"start": v(5.8, 5.08) * mm, "end": v(6.15, 3.8) * mm});
            skLineSegment(sketch, "E370", {"start": v(6.15, 3.8) * mm, "end": v(6.15, 3.37) * mm});
            skLineSegment(sketch, "E371", {"start": v(6.15, 3.37) * mm, "end": v(6.15, 3.06) * mm});
            skLineSegment(sketch, "E372", {"start": v(6.15, 3.06) * mm, "end": v(5.97, 2.14) * mm});
            skLineSegment(sketch, "E373", {"start": v(5.97, 2.14) * mm, "end": v(5.38, 0.91) * mm});
            skLineSegment(sketch, "E374", {"start": v(5.38, 0.91) * mm, "end": v(4.26, -0.2) * mm});
            skLineSegment(sketch, "E375", {"start": v(4.26, -0.2) * mm, "end": v(2.96, -0.9) * mm});
            skLineSegment(sketch, "E376", {"start": v(2.96, -0.9) * mm, "end": v(2.5, -1.07) * mm});
            skLineSegment(sketch, "E377", {"start": v(2.5, -1.07) * mm, "end": v(2.55, -1.18) * mm});
            skLineSegment(sketch, "E378", {"start": v(2.55, -1.18) * mm, "end": v(3.11, -2.32) * mm});
            skLineSegment(sketch, "E379", {"start": v(3.11, -2.32) * mm, "end": v(3.16, -2.43) * mm});
            skLineSegment(sketch, "E380", {"start": v(3.16, -2.43) * mm, "end": v(3.2, -2.42) * mm});
            skLineSegment(sketch, "E381", {"start": v(3.2, -2.42) * mm, "end": v(3.57, -2.32) * mm});
            skLineSegment(sketch, "E382", {"start": v(3.57, -2.32) * mm, "end": v(3.6, -2.3) * mm});
            skLineSegment(sketch, "E383", {"start": v(3.6, -2.3) * mm, "end": v(3.94, -2.69) * mm});
            skLineSegment(sketch, "E384", {"start": v(3.94, -2.69) * mm, "end": v(5.34, -5.13) * mm});
            skLineSegment(sketch, "E385", {"start": v(5.34, -5.13) * mm, "end": v(6.24, -7.93) * mm});
            skLineSegment(sketch, "E386", {"start": v(6.24, -7.93) * mm, "end": v(6.32, -8.5) * mm});
            skLineSegment(sketch, "E387", {"start": v(6.32, -8.5) * mm, "end": v(6.35, -8.75) * mm});
            skLineSegment(sketch, "E388", {"start": v(6.35, -8.75) * mm, "end": v(6.35, -9.56) * mm});
            skLineSegment(sketch, "E389", {"start": v(6.35, -9.56) * mm, "end": v(6.19, -10.36) * mm});
            skLineSegment(sketch, "E390", {"start": v(6.19, -10.36) * mm, "end": v(5.9, -10.93) * mm});
            skLineSegment(sketch, "E391", {"start": v(5.9, -10.93) * mm, "end": v(5.68, -11.22) * mm});
            skLineSegment(sketch, "E392", {"start": v(5.68, -11.22) * mm, "end": v(5.6, -11.3) * mm});
            skLineSegment(sketch, "E393", {"start": v(5.6, -11.3) * mm, "end": v(10, -11.3) * mm});
            skLineSegment(sketch, "E394", {"start": v(5.04, -8.73) * mm, "end": v(4.93, -8.63) * mm});
            skLineSegment(sketch, "E395", {"start": v(4.93, -8.63) * mm, "end": v(4.38, -7.94) * mm});
            skLineSegment(sketch, "E396", {"start": v(4.38, -7.94) * mm, "end": v(3.92, -6.86) * mm});
            skLineSegment(sketch, "E397", {"start": v(3.92, -6.86) * mm, "end": v(3.86, -6.57) * mm});
            skLineSegment(sketch, "E398", {"start": v(3.86, -6.57) * mm, "end": v(3.74, -6.03) * mm});
            skLineSegment(sketch, "E399", {"start": v(3.74, -6.03) * mm, "end": v(2.75, -2.9) * mm});
            skLineSegment(sketch, "E400", {"start": v(2.75, -2.9) * mm, "end": v(1.05, 0.23) * mm});
            skLineSegment(sketch, "E401", {"start": v(1.05, 0.23) * mm, "end": v(0.58, 0.77) * mm});
            skLineSegment(sketch, "E402", {"start": v(0.58, 0.77) * mm, "end": v(0.6, 0.78) * mm});
            skLineSegment(sketch, "E403", {"start": v(0.6, 0.78) * mm, "end": v(0.79, 0.87) * mm});
            skLineSegment(sketch, "E404", {"start": v(0.79, 0.87) * mm, "end": v(0.81, 0.87) * mm});
            skLineSegment(sketch, "E405", {"start": v(0.81, 0.87) * mm, "end": v(1.2, 1.07) * mm});
            skLineSegment(sketch, "E406", {"start": v(1.2, 1.07) * mm, "end": v(2.25, 1.82) * mm});
            skLineSegment(sketch, "E407", {"start": v(2.25, 1.82) * mm, "end": v(3.33, 3.01) * mm});
            skLineSegment(sketch, "E408", {"start": v(3.33, 3.01) * mm, "end": v(4, 4.41) * mm});
            skLineSegment(sketch, "E409", {"start": v(4, 4.41) * mm, "end": v(4.25, 5.6) * mm});
            skLineSegment(sketch, "E410", {"start": v(4.25, 5.6) * mm, "end": v(4.25, 6) * mm});
            skLineSegment(sketch, "E411", {"start": v(4.25, 6) * mm, "end": v(4.25, 6.29) * mm});
            skLineSegment(sketch, "E412", {"start": v(4.25, 6.29) * mm, "end": v(4.11, 7.16) * mm});
            skLineSegment(sketch, "E413", {"start": v(4.11, 7.16) * mm, "end": v(3.7, 8.28) * mm});
            skLineSegment(sketch, "E414", {"start": v(3.7, 8.28) * mm, "end": v(3, 9.29) * mm});
            skLineSegment(sketch, "E415", {"start": v(3, 9.29) * mm, "end": v(2.33, 9.94) * mm});
            skLineSegment(sketch, "E416", {"start": v(2.33, 9.94) * mm, "end": v(2.07, 10.11) * mm});
            skLineSegment(sketch, "E417", {"start": v(2.07, 10.11) * mm, "end": v(1.8, 10.3) * mm});
            skLineSegment(sketch, "E418", {"start": v(1.8, 10.3) * mm, "end": v(0.11, 10.92) * mm});
            skLineSegment(sketch, "E419", {"start": v(0.11, 10.92) * mm, "end": v(-1.8, 11.16) * mm});
            skLineSegment(sketch, "E420", {"start": v(-1.8, 11.16) * mm, "end": v(-2.43, 11.16) * mm});
            skLineSegment(sketch, "E421", {"start": v(-2.43, 11.16) * mm, "end": v(-9.62, 11.16) * mm});
            skLineSegment(sketch, "E422", {"start": v(-9.62, 11.16) * mm, "end": v(-9.52, 11.1) * mm});
            skLineSegment(sketch, "E423", {"start": v(-9.52, 11.1) * mm, "end": v(-9.21, 10.87) * mm});
            skLineSegment(sketch, "E424", {"start": v(-9.21, 10.87) * mm, "end": v(-8.79, 10.43) * mm});
            skLineSegment(sketch, "E425", {"start": v(-8.79, 10.43) * mm, "end": v(-8.46, 9.71) * mm});
            skLineSegment(sketch, "E426", {"start": v(-8.46, 9.71) * mm, "end": v(-8.32, 8.9) * mm});
            skLineSegment(sketch, "E427", {"start": v(-8.32, 8.9) * mm, "end": v(-8.32, 8.62) * mm});
            skLineSegment(sketch, "E428", {"start": v(-8.32, 8.62) * mm, "end": v(-8.32, -6.19) * mm});
            skLineSegment(sketch, "E429", {"start": v(-8.32, -6.19) * mm, "end": v(-8.32, -6.46) * mm});
            skLineSegment(sketch, "E430", {"start": v(-8.32, -6.46) * mm, "end": v(-8.46, -7.29) * mm});
            skLineSegment(sketch, "E431", {"start": v(-8.46, -7.29) * mm, "end": v(-8.79, -8) * mm});
            skLineSegment(sketch, "E432", {"start": v(-8.79, -8) * mm, "end": v(-9.21, -8.44) * mm});
            skLineSegment(sketch, "E433", {"start": v(-9.21, -8.44) * mm, "end": v(-9.52, -8.66) * mm});
            skLineSegment(sketch, "E434", {"start": v(-9.52, -8.66) * mm, "end": v(-9.62, -8.73) * mm});
            skLineSegment(sketch, "E435", {"start": v(-9.62, -8.73) * mm, "end": v(-4.63, -8.73) * mm});
            skLineSegment(sketch, "E436", {"start": v(-4.63, -8.73) * mm, "end": v(-4.73, -8.66) * mm});
            skLineSegment(sketch, "E437", {"start": v(-4.73, -8.66) * mm, "end": v(-5.03, -8.44) * mm});
            skLineSegment(sketch, "E438", {"start": v(-5.03, -8.44) * mm, "end": v(-5.46, -8) * mm});
            skLineSegment(sketch, "E439", {"start": v(-5.46, -8) * mm, "end": v(-5.8, -7.29) * mm});
            skLineSegment(sketch, "E440", {"start": v(-5.8, -7.29) * mm, "end": v(-5.93, -6.46) * mm});
            skLineSegment(sketch, "E441", {"start": v(-5.93, -6.46) * mm, "end": v(-5.93, -6.19) * mm});
            skLineSegment(sketch, "E442", {"start": v(-5.93, -6.19) * mm, "end": v(-5.93, -0.45) * mm});
            skLineSegment(sketch, "E443", {"start": v(-5.93, -0.45) * mm, "end": v(-5.3, -0.45) * mm});
            skLineSegment(sketch, "E444", {"start": v(-5.3, -0.45) * mm, "end": v(-3.4, -0.3) * mm});
            skLineSegment(sketch, "E445", {"start": v(-3.4, -0.3) * mm, "end": v(-1.5, 0.04) * mm});
            skLineSegment(sketch, "E446", {"start": v(-1.5, 0.04) * mm, "end": v(-1.15, 0.13) * mm});
            skLineSegment(sketch, "E447", {"start": v(-1.15, 0.13) * mm, "end": v(-0.84, -0.25) * mm});
            skLineSegment(sketch, "E448", {"start": v(-0.84, -0.25) * mm, "end": v(0.46, -2.64) * mm});
            skLineSegment(sketch, "E449", {"start": v(0.46, -2.64) * mm, "end": v(1.27, -5.35) * mm});
            skLineSegment(sketch, "E450", {"start": v(1.27, -5.35) * mm, "end": v(1.34, -5.89) * mm});
            skLineSegment(sketch, "E451", {"start": v(1.34, -5.89) * mm, "end": v(1.38, -6.15) * mm});
            skLineSegment(sketch, "E452", {"start": v(1.38, -6.15) * mm, "end": v(1.37, -6.96) * mm});
            skLineSegment(sketch, "E453", {"start": v(1.37, -6.96) * mm, "end": v(1.2, -7.77) * mm});
            skLineSegment(sketch, "E454", {"start": v(1.2, -7.77) * mm, "end": v(0.92, -8.35) * mm});
            skLineSegment(sketch, "E455", {"start": v(0.92, -8.35) * mm, "end": v(0.7, -8.64) * mm});
            skLineSegment(sketch, "E456", {"start": v(0.7, -8.64) * mm, "end": v(0.62, -8.73) * mm});
            skLineSegment(sketch, "E457", {"start": v(0.62, -8.73) * mm, "end": v(5.04, -8.73) * mm});
            skLineSegment(sketch, "E458", {"start": v(-5.93, 0.87) * mm, "end": v(-5.93, 9.84) * mm});
            skLineSegment(sketch, "E459", {"start": v(-5.93, 9.84) * mm, "end": v(-2.54, 9.84) * mm});
            skLineSegment(sketch, "E460", {"start": v(-2.54, 9.84) * mm, "end": v(-2.23, 9.83) * mm});
            skLineSegment(sketch, "E461", {"start": v(-2.23, 9.83) * mm, "end": v(-0.9, 9.63) * mm});
            skLineSegment(sketch, "E462", {"start": v(-0.9, 9.63) * mm, "end": v(0.16, 9.17) * mm});
            skLineSegment(sketch, "E463", {"start": v(0.16, 9.17) * mm, "end": v(0.34, 9.05) * mm});
            skLineSegment(sketch, "E464", {"start": v(0.34, 9.05) * mm, "end": v(0.58, 8.88) * mm});
            skLineSegment(sketch, "E465", {"start": v(0.58, 8.88) * mm, "end": v(1.44, 7.74) * mm});
            skLineSegment(sketch, "E466", {"start": v(1.44, 7.74) * mm, "end": v(1.81, 6.42) * mm});
            skLineSegment(sketch, "E467", {"start": v(1.81, 6.42) * mm, "end": v(1.81, 5.98) * mm});
            skLineSegment(sketch, "E468", {"start": v(1.81, 5.98) * mm, "end": v(1.81, 5.55) * mm});
            skLineSegment(sketch, "E469", {"start": v(1.81, 5.55) * mm, "end": v(1.48, 4.27) * mm});
            skLineSegment(sketch, "E470", {"start": v(1.48, 4.27) * mm, "end": v(0.28, 2.64) * mm});
            skLineSegment(sketch, "E471", {"start": v(0.28, 2.64) * mm, "end": v(-2.1, 1.4) * mm});
            skLineSegment(sketch, "E472", {"start": v(-2.1, 1.4) * mm, "end": v(-4.97, 0.9) * mm});
            skLineSegment(sketch, "E473", {"start": v(-4.97, 0.9) * mm, "end": v(-5.93, 0.87) * mm});
            skLineSegment(sketch, "E474", {"start": v(-1.6, 2.16) * mm, "end": v(-1.6, 7.21) * mm});
            skLineSegment(sketch, "E475", {"start": v(-1.6, 7.21) * mm, "end": v(1.09, 7.21) * mm});
            skLineSegment(sketch, "E476", {"start": v(1.09, 7.21) * mm, "end": v(1.04, 7.35) * mm});
            skLineSegment(sketch, "E477", {"start": v(1.04, 7.35) * mm, "end": v(0.69, 7.96) * mm});
            skLineSegment(sketch, "E478", {"start": v(0.69, 7.96) * mm, "end": v(0.2, 8.47) * mm});
            skLineSegment(sketch, "E479", {"start": v(0.2, 8.47) * mm, "end": v(0.09, 8.56) * mm});
            skLineSegment(sketch, "E480", {"start": v(0.09, 8.56) * mm, "end": v(-5.3, 8.56) * mm});
            skLineSegment(sketch, "E481", {"start": v(-5.3, 8.56) * mm, "end": v(-5.19, 8.49) * mm});
            skLineSegment(sketch, "E482", {"start": v(-5.19, 8.49) * mm, "end": v(-4.88, 8.28) * mm});
            skLineSegment(sketch, "E483", {"start": v(-4.88, 8.28) * mm, "end": v(-4.46, 7.83) * mm});
            skLineSegment(sketch, "E484", {"start": v(-4.46, 7.83) * mm, "end": v(-4.12, 7.12) * mm});
            skLineSegment(sketch, "E485", {"start": v(-4.12, 7.12) * mm, "end": v(-3.99, 6.3) * mm});
            skLineSegment(sketch, "E486", {"start": v(-3.99, 6.3) * mm, "end": v(-3.99, 6.02) * mm});
            skLineSegment(sketch, "E487", {"start": v(-3.99, 6.02) * mm, "end": v(-3.99, 1.56) * mm});
            skLineSegment(sketch, "E488", {"start": v(-3.99, 1.56) * mm, "end": v(-3.77, 1.6) * mm});
            skLineSegment(sketch, "E489", {"start": v(-3.77, 1.6) * mm, "end": v(-1.77, 2.09) * mm});
            skLineSegment(sketch, "E490", {"start": v(-1.77, 2.09) * mm, "end": v(-1.6, 2.16) * mm});
            skLineSegment(sketch, "E491", {"start": v(3.28, -16.86) * mm, "end": v(3.28, -16.98) * mm});
            skLineSegment(sketch, "E492", {"start": v(3.28, -16.98) * mm, "end": v(3.36, -17.36) * mm});
            skLineSegment(sketch, "E493", {"start": v(3.36, -17.36) * mm, "end": v(3.6, -17.77) * mm});
            skLineSegment(sketch, "E494", {"start": v(3.6, -17.77) * mm, "end": v(3.96, -18.04) * mm});
            skLineSegment(sketch, "E495", {"start": v(3.96, -18.04) * mm, "end": v(4.33, -18.14) * mm});
            skLineSegment(sketch, "E496", {"start": v(4.33, -18.14) * mm, "end": v(4.46, -18.14) * mm});
            skLineSegment(sketch, "E497", {"start": v(4.46, -18.14) * mm, "end": v(4.64, -18.14) * mm});
            skLineSegment(sketch, "E498", {"start": v(4.64, -18.14) * mm, "end": v(5.2, -18.03) * mm});
            skLineSegment(sketch, "E499", {"start": v(5.2, -18.03) * mm, "end": v(5.64, -17.8) * mm});
            skLineSegment(sketch, "E500", {"start": v(5.64, -17.8) * mm, "end": v(5.7, -17.73) * mm});
            skLineSegment(sketch, "E501", {"start": v(5.7, -17.73) * mm, "end": v(5.57, -18.56) * mm});
            skLineSegment(sketch, "E502", {"start": v(5.57, -18.56) * mm, "end": v(5.52, -18.58) * mm});
            skLineSegment(sketch, "E503", {"start": v(5.52, -18.58) * mm, "end": v(5.16, -18.7) * mm});
            skLineSegment(sketch, "E504", {"start": v(5.16, -18.7) * mm, "end": v(4.65, -18.76) * mm});
            skLineSegment(sketch, "E505", {"start": v(4.65, -18.76) * mm, "end": v(4.48, -18.76) * mm});
            skLineSegment(sketch, "E506", {"start": v(4.48, -18.76) * mm, "end": v(4.27, -18.76) * mm});
            skLineSegment(sketch, "E507", {"start": v(4.27, -18.76) * mm, "end": v(3.66, -18.63) * mm});
            skLineSegment(sketch, "E508", {"start": v(3.66, -18.63) * mm, "end": v(3.02, -18.25) * mm});
            skLineSegment(sketch, "E509", {"start": v(3.02, -18.25) * mm, "end": v(2.6, -17.66) * mm});
            skLineSegment(sketch, "E510", {"start": v(2.6, -17.66) * mm, "end": v(2.45, -17.06) * mm});
            skLineSegment(sketch, "E511", {"start": v(2.45, -17.06) * mm, "end": v(2.45, -16.86) * mm});
            skLineSegment(sketch, "E512", {"start": v(2.45, -16.86) * mm, "end": v(2.45, -16.64) * mm});
            skLineSegment(sketch, "E513", {"start": v(2.45, -16.64) * mm, "end": v(2.63, -16.01) * mm});
            skLineSegment(sketch, "E514", {"start": v(2.63, -16.01) * mm, "end": v(3, -15.48) * mm});
            skLineSegment(sketch, "E515", {"start": v(3, -15.48) * mm, "end": v(3.1, -15.4) * mm});
            skLineSegment(sketch, "E516", {"start": v(3.1, -15.4) * mm, "end": v(3.18, -15.33) * mm});
            skLineSegment(sketch, "E517", {"start": v(3.18, -15.33) * mm, "end": v(3.7, -15.06) * mm});
            skLineSegment(sketch, "E518", {"start": v(3.7, -15.06) * mm, "end": v(4.29, -14.94) * mm});
            skLineSegment(sketch, "E519", {"start": v(4.29, -14.94) * mm, "end": v(4.48, -14.94) * mm});
            skLineSegment(sketch, "E520", {"start": v(4.48, -14.94) * mm, "end": v(4.65, -14.94) * mm});
            skLineSegment(sketch, "E521", {"start": v(4.65, -14.94) * mm, "end": v(5.16, -15) * mm});
            skLineSegment(sketch, "E522", {"start": v(5.16, -15) * mm, "end": v(5.52, -15.12) * mm});
            skLineSegment(sketch, "E523", {"start": v(5.52, -15.12) * mm, "end": v(5.57, -15.15) * mm});
            skLineSegment(sketch, "E524", {"start": v(5.57, -15.15) * mm, "end": v(5.57, -15.94) * mm});
            skLineSegment(sketch, "E525", {"start": v(5.57, -15.94) * mm, "end": v(5.51, -15.87) * mm});
            skLineSegment(sketch, "E526", {"start": v(5.51, -15.87) * mm, "end": v(5.13, -15.65) * mm});
            skLineSegment(sketch, "E527", {"start": v(5.13, -15.65) * mm, "end": v(4.63, -15.55) * mm});
            skLineSegment(sketch, "E528", {"start": v(4.63, -15.55) * mm, "end": v(4.46, -15.55) * mm});
            skLineSegment(sketch, "E529", {"start": v(4.46, -15.55) * mm, "end": v(4.33, -15.55) * mm});
            skLineSegment(sketch, "E530", {"start": v(4.33, -15.55) * mm, "end": v(3.96, -15.65) * mm});
            skLineSegment(sketch, "E531", {"start": v(3.96, -15.65) * mm, "end": v(3.6, -15.92) * mm});
            skLineSegment(sketch, "E532", {"start": v(3.6, -15.92) * mm, "end": v(3.36, -16.34) * mm});
            skLineSegment(sketch, "E533", {"start": v(3.36, -16.34) * mm, "end": v(3.28, -16.73) * mm});
            skLineSegment(sketch, "E534", {"start": v(3.28, -16.73) * mm, "end": v(3.28, -16.86) * mm});
            skLineSegment(sketch, "E535", {"start": v(-6.38, -17.75) * mm, "end": v(-6.42, -17.67) * mm});
            skLineSegment(sketch, "E536", {"start": v(-6.42, -17.67) * mm, "end": v(-6.64, -17.3) * mm});
            skLineSegment(sketch, "E537", {"start": v(-6.64, -17.3) * mm, "end": v(-6.9, -17.05) * mm});
            skLineSegment(sketch, "E538", {"start": v(-6.9, -17.05) * mm, "end": v(-6.96, -17.03) * mm});
            skLineSegment(sketch, "E539", {"start": v(-6.96, -17.03) * mm, "end": v(-6.82, -17) * mm});
            skLineSegment(sketch, "E540", {"start": v(-6.82, -17) * mm, "end": v(-6.33, -16.7) * mm});
            skLineSegment(sketch, "E541", {"start": v(-6.33, -16.7) * mm, "end": v(-6.1, -16.23) * mm});
            skLineSegment(sketch, "E542", {"start": v(-6.1, -16.23) * mm, "end": v(-6.1, -16.1) * mm});
            skLineSegment(sketch, "E543", {"start": v(-6.1, -16.1) * mm, "end": v(-6.1, -15.95) * mm});
            skLineSegment(sketch, "E544", {"start": v(-6.1, -15.95) * mm, "end": v(-6.26, -15.48) * mm});
            skLineSegment(sketch, "E545", {"start": v(-6.26, -15.48) * mm, "end": v(-6.6, -15.14) * mm});
            skLineSegment(sketch, "E546", {"start": v(-6.6, -15.14) * mm, "end": v(-6.7, -15.1) * mm});
            skLineSegment(sketch, "E547", {"start": v(-6.7, -15.1) * mm, "end": v(-6.76, -15.09) * mm});
            skLineSegment(sketch, "E548", {"start": v(-6.76, -15.09) * mm, "end": v(-7.48, -15.02) * mm});
            skLineSegment(sketch, "E549", {"start": v(-7.48, -15.02) * mm, "end": v(-7.72, -15.02) * mm});
            skLineSegment(sketch, "E550", {"start": v(-7.72, -15.02) * mm, "end": v(-9.58, -15.02) * mm});
            skLineSegment(sketch, "E551", {"start": v(-9.58, -15.02) * mm, "end": v(-9.54, -15.05) * mm});
            skLineSegment(sketch, "E552", {"start": v(-9.54, -15.05) * mm, "end": v(-9.38, -15.34) * mm});
            skLineSegment(sketch, "E553", {"start": v(-9.38, -15.34) * mm, "end": v(-9.3, -15.7) * mm});
            skLineSegment(sketch, "E554", {"start": v(-9.3, -15.7) * mm, "end": v(-9.3, -15.83) * mm});
            skLineSegment(sketch, "E555", {"start": v(-9.3, -15.83) * mm, "end": v(-9.3, -17.88) * mm});
            skLineSegment(sketch, "E556", {"start": v(-9.3, -17.88) * mm, "end": v(-9.3, -18) * mm});
            skLineSegment(sketch, "E557", {"start": v(-9.3, -18) * mm, "end": v(-9.38, -18.35) * mm});
            skLineSegment(sketch, "E558", {"start": v(-9.38, -18.35) * mm, "end": v(-9.54, -18.66) * mm});
            skLineSegment(sketch, "E559", {"start": v(-9.54, -18.66) * mm, "end": v(-9.58, -18.7) * mm});
            skLineSegment(sketch, "E560", {"start": v(-9.58, -18.7) * mm, "end": v(-8.26, -18.7) * mm});
            skLineSegment(sketch, "E561", {"start": v(-8.26, -18.7) * mm, "end": v(-8.3, -18.66) * mm});
            skLineSegment(sketch, "E562", {"start": v(-8.3, -18.66) * mm, "end": v(-8.46, -18.35) * mm});
            skLineSegment(sketch, "E563", {"start": v(-8.46, -18.35) * mm, "end": v(-8.53, -18) * mm});
            skLineSegment(sketch, "E564", {"start": v(-8.53, -18) * mm, "end": v(-8.53, -17.88) * mm});
            skLineSegment(sketch, "E565", {"start": v(-8.53, -17.88) * mm, "end": v(-8.53, -17.22) * mm});
            skLineSegment(sketch, "E566", {"start": v(-8.53, -17.22) * mm, "end": v(-7.98, -17.22) * mm});
            skLineSegment(sketch, "E567", {"start": v(-7.98, -17.22) * mm, "end": v(-7.89, -17.22) * mm});
            skLineSegment(sketch, "E568", {"start": v(-7.89, -17.22) * mm, "end": v(-7.62, -17.3) * mm});
            skLineSegment(sketch, "E569", {"start": v(-7.62, -17.3) * mm, "end": v(-7.41, -17.5) * mm});
            skLineSegment(sketch, "E570", {"start": v(-7.41, -17.5) * mm, "end": v(-7.38, -17.56) * mm});
            skLineSegment(sketch, "E571", {"start": v(-7.38, -17.56) * mm, "end": v(-7.34, -17.64) * mm});
            skLineSegment(sketch, "E572", {"start": v(-7.34, -17.64) * mm, "end": v(-6.87, -18.58) * mm});
            skLineSegment(sketch, "E573", {"start": v(-6.87, -18.58) * mm, "end": v(-6.8, -18.67) * mm});
            skLineSegment(sketch, "E574", {"start": v(-6.8, -18.67) * mm, "end": v(-5.72, -18.7) * mm});
            skLineSegment(sketch, "E575", {"start": v(-5.72, -18.7) * mm, "end": v(-5.8, -18.63) * mm});
            skLineSegment(sketch, "E576", {"start": v(-5.8, -18.63) * mm, "end": v(-6.12, -18.26) * mm});
            skLineSegment(sketch, "E577", {"start": v(-6.12, -18.26) * mm, "end": v(-6.34, -17.84) * mm});
            skLineSegment(sketch, "E578", {"start": v(-6.34, -17.84) * mm, "end": v(-6.38, -17.75) * mm});
            skLineSegment(sketch, "E579", {"start": v(-6.91, -16.13) * mm, "end": v(-6.91, -16.23) * mm});
            skLineSegment(sketch, "E580", {"start": v(-6.91, -16.23) * mm, "end": v(-7.12, -16.52) * mm});
            skLineSegment(sketch, "E581", {"start": v(-7.12, -16.52) * mm, "end": v(-7.54, -16.64) * mm});
            skLineSegment(sketch, "E582", {"start": v(-7.54, -16.64) * mm, "end": v(-7.68, -16.64) * mm});
            skLineSegment(sketch, "E583", {"start": v(-7.68, -16.64) * mm, "end": v(-8.53, -16.64) * mm});
            skLineSegment(sketch, "E584", {"start": v(-8.53, -16.64) * mm, "end": v(-8.53, -15.62) * mm});
            skLineSegment(sketch, "E585", {"start": v(-8.53, -15.62) * mm, "end": v(-7.68, -15.62) * mm});
            skLineSegment(sketch, "E586", {"start": v(-7.68, -15.62) * mm, "end": v(-7.54, -15.62) * mm});
            skLineSegment(sketch, "E587", {"start": v(-7.54, -15.62) * mm, "end": v(-7.12, -15.73) * mm});
            skLineSegment(sketch, "E588", {"start": v(-7.12, -15.73) * mm, "end": v(-6.91, -16.03) * mm});
            skLineSegment(sketch, "E589", {"start": v(-6.91, -16.03) * mm, "end": v(-6.91, -16.13) * mm});
            skLineSegment(sketch, "E590", {"start": v(-4.3, -17.82) * mm, "end": v(-4.36, -17.77) * mm});
            skLineSegment(sketch, "E591", {"start": v(-4.36, -17.77) * mm, "end": v(-4.55, -17.43) * mm});
            skLineSegment(sketch, "E592", {"start": v(-4.55, -17.43) * mm, "end": v(-4.63, -17) * mm});
            skLineSegment(sketch, "E593", {"start": v(-4.63, -17) * mm, "end": v(-4.63, -16.86) * mm});
            skLineSegment(sketch, "E594", {"start": v(-4.63, -16.86) * mm, "end": v(-4.63, -16.71) * mm});
            skLineSegment(sketch, "E595", {"start": v(-4.63, -16.71) * mm, "end": v(-4.55, -16.28) * mm});
            skLineSegment(sketch, "E596", {"start": v(-4.55, -16.28) * mm, "end": v(-4.36, -15.93) * mm});
            skLineSegment(sketch, "E597", {"start": v(-4.36, -15.93) * mm, "end": v(-4.3, -15.88) * mm});
            skLineSegment(sketch, "E598", {"start": v(-4.3, -15.88) * mm, "end": v(-4.26, -15.83) * mm});
            skLineSegment(sketch, "E599", {"start": v(-4.26, -15.83) * mm, "end": v(-3.7, -15.58) * mm});
            skLineSegment(sketch, "E600", {"start": v(-3.7, -15.58) * mm, "end": v(-3.52, -15.58) * mm});
            skLineSegment(sketch, "E601", {"start": v(-3.52, -15.58) * mm, "end": v(-3.33, -15.58) * mm});
            skLineSegment(sketch, "E602", {"start": v(-3.33, -15.58) * mm, "end": v(-2.8, -15.83) * mm});
            skLineSegment(sketch, "E603", {"start": v(-2.8, -15.83) * mm, "end": v(-2.75, -15.88) * mm});
            skLineSegment(sketch, "E604", {"start": v(-2.75, -15.88) * mm, "end": v(-2.7, -15.93) * mm});
            skLineSegment(sketch, "E605", {"start": v(-2.7, -15.93) * mm, "end": v(-2.43, -16.62) * mm});
            skLineSegment(sketch, "E606", {"start": v(-2.43, -16.62) * mm, "end": v(-2.43, -16.86) * mm});
            skLineSegment(sketch, "E607", {"start": v(-2.43, -16.86) * mm, "end": v(-2.43, -17.1) * mm});
            skLineSegment(sketch, "E608", {"start": v(-2.43, -17.1) * mm, "end": v(-2.7, -17.77) * mm});
            skLineSegment(sketch, "E609", {"start": v(-2.7, -17.77) * mm, "end": v(-2.75, -17.82) * mm});
            skLineSegment(sketch, "E610", {"start": v(-2.75, -17.82) * mm, "end": v(-2.8, -17.86) * mm});
            skLineSegment(sketch, "E611", {"start": v(-2.8, -17.86) * mm, "end": v(-3.34, -18.14) * mm});
            skLineSegment(sketch, "E612", {"start": v(-3.34, -18.14) * mm, "end": v(-3.52, -18.14) * mm});
            skLineSegment(sketch, "E613", {"start": v(-3.52, -18.14) * mm, "end": v(-3.72, -18.14) * mm});
            skLineSegment(sketch, "E614", {"start": v(-3.72, -18.14) * mm, "end": v(-4.26, -17.86) * mm});
            skLineSegment(sketch, "E615", {"start": v(-4.26, -17.86) * mm, "end": v(-4.3, -17.82) * mm});
            skLineSegment(sketch, "E616", {"start": v(-3.54, -18.78) * mm, "end": v(-3.37, -18.78) * mm});
            skLineSegment(sketch, "E617", {"start": v(-3.37, -18.78) * mm, "end": v(-2.84, -18.67) * mm});
            skLineSegment(sketch, "E618", {"start": v(-2.84, -18.67) * mm, "end": v(-2.36, -18.42) * mm});
            skLineSegment(sketch, "E619", {"start": v(-2.36, -18.42) * mm, "end": v(-2.28, -18.35) * mm});
            skLineSegment(sketch, "E620", {"start": v(-2.28, -18.35) * mm, "end": v(-2.19, -18.27) * mm});
            skLineSegment(sketch, "E621", {"start": v(-2.19, -18.27) * mm, "end": v(-1.8, -17.74) * mm});
            skLineSegment(sketch, "E622", {"start": v(-1.8, -17.74) * mm, "end": v(-1.62, -17.08) * mm});
            skLineSegment(sketch, "E623", {"start": v(-1.62, -17.08) * mm, "end": v(-1.62, -16.86) * mm});
            skLineSegment(sketch, "E624", {"start": v(-1.62, -16.86) * mm, "end": v(-1.62, -16.63) * mm});
            skLineSegment(sketch, "E625", {"start": v(-1.62, -16.63) * mm, "end": v(-1.8, -15.97) * mm});
            skLineSegment(sketch, "E626", {"start": v(-1.8, -15.97) * mm, "end": v(-2.19, -15.43) * mm});
            skLineSegment(sketch, "E627", {"start": v(-2.19, -15.43) * mm, "end": v(-2.28, -15.34) * mm});
            skLineSegment(sketch, "E628", {"start": v(-2.28, -15.34) * mm, "end": v(-2.36, -15.28) * mm});
            skLineSegment(sketch, "E629", {"start": v(-2.36, -15.28) * mm, "end": v(-2.84, -15.04) * mm});
            skLineSegment(sketch, "E630", {"start": v(-2.84, -15.04) * mm, "end": v(-3.37, -14.94) * mm});
            skLineSegment(sketch, "E631", {"start": v(-3.37, -14.94) * mm, "end": v(-3.54, -14.94) * mm});
            skLineSegment(sketch, "E632", {"start": v(-3.54, -14.94) * mm, "end": v(-3.71, -14.94) * mm});
            skLineSegment(sketch, "E633", {"start": v(-3.71, -14.94) * mm, "end": v(-4.23, -15.04) * mm});
            skLineSegment(sketch, "E634", {"start": v(-4.23, -15.04) * mm, "end": v(-4.7, -15.28) * mm});
            skLineSegment(sketch, "E635", {"start": v(-4.7, -15.28) * mm, "end": v(-4.78, -15.34) * mm});
            skLineSegment(sketch, "E636", {"start": v(-4.78, -15.34) * mm, "end": v(-4.88, -15.43) * mm});
            skLineSegment(sketch, "E637", {"start": v(-4.88, -15.43) * mm, "end": v(-5.26, -15.97) * mm});
            skLineSegment(sketch, "E638", {"start": v(-5.26, -15.97) * mm, "end": v(-5.44, -16.63) * mm});
            skLineSegment(sketch, "E639", {"start": v(-5.44, -16.63) * mm, "end": v(-5.44, -16.86) * mm});
            skLineSegment(sketch, "E640", {"start": v(-5.44, -16.86) * mm, "end": v(-5.44, -17.08) * mm});
            skLineSegment(sketch, "E641", {"start": v(-5.44, -17.08) * mm, "end": v(-5.26, -17.74) * mm});
            skLineSegment(sketch, "E642", {"start": v(-5.26, -17.74) * mm, "end": v(-4.88, -18.27) * mm});
            skLineSegment(sketch, "E643", {"start": v(-4.88, -18.27) * mm, "end": v(-4.78, -18.35) * mm});
            skLineSegment(sketch, "E644", {"start": v(-4.78, -18.35) * mm, "end": v(-4.7, -18.42) * mm});
            skLineSegment(sketch, "E645", {"start": v(-4.7, -18.42) * mm, "end": v(-4.23, -18.67) * mm});
            skLineSegment(sketch, "E646", {"start": v(-4.23, -18.67) * mm, "end": v(-3.71, -18.78) * mm});
            skLineSegment(sketch, "E647", {"start": v(-3.71, -18.78) * mm, "end": v(-3.54, -18.78) * mm});
            skLineSegment(sketch, "E648", {"start": v(1.24, -15.02) * mm, "end": v(1.26, -15.04) * mm});
            skLineSegment(sketch, "E649", {"start": v(1.26, -15.04) * mm, "end": v(1.35, -15.21) * mm});
            skLineSegment(sketch, "E650", {"start": v(1.35, -15.21) * mm, "end": v(1.34, -15.24) * mm});
            skLineSegment(sketch, "E651", {"start": v(1.34, -15.24) * mm, "end": v(1.24, -15.54) * mm});
            skLineSegment(sketch, "E652", {"start": v(1.24, -15.54) * mm, "end": v(1.22, -15.58) * mm});
            skLineSegment(sketch, "E653", {"start": v(1.22, -15.58) * mm, "end": v(0.5, -16.62) * mm});
            skLineSegment(sketch, "E654", {"start": v(0.5, -16.62) * mm, "end": v(-0.23, -15.55) * mm});
            skLineSegment(sketch, "E655", {"start": v(-0.23, -15.55) * mm, "end": v(-0.26, -15.52) * mm});
            skLineSegment(sketch, "E656", {"start": v(-0.26, -15.52) * mm, "end": v(-0.39, -15.22) * mm});
            skLineSegment(sketch, "E657", {"start": v(-0.39, -15.22) * mm, "end": v(-0.38, -15.2) * mm});
            skLineSegment(sketch, "E658", {"start": v(-0.38, -15.2) * mm, "end": v(-0.38, -15.18) * mm});
            skLineSegment(sketch, "E659", {"start": v(-0.38, -15.18) * mm, "end": v(-0.28, -15.03) * mm});
            skLineSegment(sketch, "E660", {"start": v(-0.28, -15.03) * mm, "end": v(-0.26, -15.02) * mm});
            skLineSegment(sketch, "E661", {"start": v(-0.26, -15.02) * mm, "end": v(-1.73, -15.02) * mm});
            skLineSegment(sketch, "E662", {"start": v(-1.73, -15.02) * mm, "end": v(-1.67, -15.05) * mm});
            skLineSegment(sketch, "E663", {"start": v(-1.67, -15.05) * mm, "end": v(-1.2, -15.53) * mm});
            skLineSegment(sketch, "E664", {"start": v(-1.2, -15.53) * mm, "end": v(-1.15, -15.6) * mm});
            skLineSegment(sketch, "E665", {"start": v(-1.15, -15.6) * mm, "end": v(0.04, -17.28) * mm});
            skLineSegment(sketch, "E666", {"start": v(0.04, -17.28) * mm, "end": v(0.04, -17.88) * mm});
            skLineSegment(sketch, "E667", {"start": v(0.04, -17.88) * mm, "end": v(0.04, -18) * mm});
            skLineSegment(sketch, "E668", {"start": v(0.04, -18) * mm, "end": v(-0.03, -18.35) * mm});
            skLineSegment(sketch, "E669", {"start": v(-0.03, -18.35) * mm, "end": v(-0.2, -18.64) * mm});
            skLineSegment(sketch, "E670", {"start": v(-0.2, -18.64) * mm, "end": v(-0.23, -18.67) * mm});
            skLineSegment(sketch, "E671", {"start": v(-0.23, -18.67) * mm, "end": v(1.09, -18.67) * mm});
            skLineSegment(sketch, "E672", {"start": v(1.09, -18.67) * mm, "end": v(1.05, -18.64) * mm});
            skLineSegment(sketch, "E673", {"start": v(1.05, -18.64) * mm, "end": v(0.89, -18.35) * mm});
            skLineSegment(sketch, "E674", {"start": v(0.89, -18.35) * mm, "end": v(0.81, -18) * mm});
            skLineSegment(sketch, "E675", {"start": v(0.81, -18) * mm, "end": v(0.81, -17.88) * mm});
            skLineSegment(sketch, "E676", {"start": v(0.81, -17.88) * mm, "end": v(0.81, -17.28) * mm});
            skLineSegment(sketch, "E677", {"start": v(0.81, -17.28) * mm, "end": v(1.9, -15.75) * mm});
            skLineSegment(sketch, "E678", {"start": v(1.9, -15.75) * mm, "end": v(1.94, -15.7) * mm});
            skLineSegment(sketch, "E679", {"start": v(1.94, -15.7) * mm, "end": v(2.2, -15.35) * mm});
            skLineSegment(sketch, "E680", {"start": v(2.2, -15.35) * mm, "end": v(2.5, -15.05) * mm});
            skLineSegment(sketch, "E681", {"start": v(2.5, -15.05) * mm, "end": v(2.56, -15.02) * mm});
            skLineSegment(sketch, "E682", {"start": v(2.56, -15.02) * mm, "end": v(1.24, -15.02) * mm});
            skLineSegment(sketch, "E683", {"start": v(8.32, -18.1) * mm, "end": v(7.38, -18.1) * mm});
            skLineSegment(sketch, "E684", {"start": v(7.38, -18.1) * mm, "end": v(7.38, -17.1) * mm});
            skLineSegment(sketch, "E685", {"start": v(7.38, -17.1) * mm, "end": v(8.8, -17.1) * mm});
            skLineSegment(sketch, "E686", {"start": v(8.8, -17.1) * mm, "end": v(8.88, -16.54) * mm});
            skLineSegment(sketch, "E687", {"start": v(8.88, -16.54) * mm, "end": v(7.38, -16.54) * mm});
            skLineSegment(sketch, "E688", {"start": v(7.38, -16.54) * mm, "end": v(7.38, -15.62) * mm});
            skLineSegment(sketch, "E689", {"start": v(7.38, -15.62) * mm, "end": v(8.22, -15.62) * mm});
            skLineSegment(sketch, "E690", {"start": v(8.22, -15.62) * mm, "end": v(8.37, -15.62) * mm});
            skLineSegment(sketch, "E691", {"start": v(8.37, -15.62) * mm, "end": v(8.84, -15.65) * mm});
            skLineSegment(sketch, "E692", {"start": v(8.84, -15.65) * mm, "end": v(9.21, -15.78) * mm});
            skLineSegment(sketch, "E693", {"start": v(9.21, -15.78) * mm, "end": v(9.26, -15.83) * mm});
            skLineSegment(sketch, "E694", {"start": v(9.26, -15.83) * mm, "end": v(9.26, -15.02) * mm});
            skLineSegment(sketch, "E695", {"start": v(9.26, -15.02) * mm, "end": v(6.34, -15.02) * mm});
            skLineSegment(sketch, "E696", {"start": v(6.34, -15.02) * mm, "end": v(6.38, -15.05) * mm});
            skLineSegment(sketch, "E697", {"start": v(6.38, -15.05) * mm, "end": v(6.54, -15.36) * mm});
            skLineSegment(sketch, "E698", {"start": v(6.54, -15.36) * mm, "end": v(6.61, -15.71) * mm});
            skLineSegment(sketch, "E699", {"start": v(6.61, -15.71) * mm, "end": v(6.61, -15.83) * mm});
            skLineSegment(sketch, "E700", {"start": v(6.61, -15.83) * mm, "end": v(6.61, -17.88) * mm});
            skLineSegment(sketch, "E701", {"start": v(6.61, -17.88) * mm, "end": v(6.61, -18) * mm});
            skLineSegment(sketch, "E702", {"start": v(6.61, -18) * mm, "end": v(6.54, -18.36) * mm});
            skLineSegment(sketch, "E703", {"start": v(6.54, -18.36) * mm, "end": v(6.38, -18.66) * mm});
            skLineSegment(sketch, "E704", {"start": v(6.38, -18.66) * mm, "end": v(6.34, -18.7) * mm});
            skLineSegment(sketch, "E705", {"start": v(6.34, -18.7) * mm, "end": v(9.28, -18.7) * mm});
            skLineSegment(sketch, "E706", {"start": v(9.28, -18.7) * mm, "end": v(9.4, -17.8) * mm});
            skLineSegment(sketch, "E707", {"start": v(9.4, -17.8) * mm, "end": v(9.36, -17.86) * mm});
            skLineSegment(sketch, "E708", {"start": v(9.36, -17.86) * mm, "end": v(8.96, -18.05) * mm});
            skLineSegment(sketch, "E709", {"start": v(8.96, -18.05) * mm, "end": v(8.48, -18.1) * mm});
            skLineSegment(sketch, "E710", {"start": v(8.48, -18.1) * mm, "end": v(8.32, -18.1) * mm});
            skSolve(sketch);
        }
        {
            var Q0;
            Q0 = qSketchRegion(id + "F2", true);
            extrude(context, id + "F3", {"entities" : qUnion([Q0]), "operationType" : NewBodyOperationType.REMOVE, "oppositeDirection" : true, "depth" : 1.27 * mm, "offsetDistance" : 25.4 * mm});
        }
        {
            var Q0;
            Q0=makeQuery(id+"F3.boolean.opBoolean","SPLIT",FACE,{"disambiguationData":[TD([makeQuery(id+"F3.opExtrude","SWEPT_FACE",FACE,{"disambiguationData":[OSD([sQuery(id+"F2.wireOp",EDGE,"E72")])]})])],"derivedFrom":makeQuery(id+"F1.opExtrude","CAP_FACE",FACE,{"disambiguationData":[OSD([sQuery(id+"F0.wireOp",EDGE,"E0"),sQuery(id+"F0.wireOp",EDGE,"E1"),sQuery(id+"F0.wireOp",EDGE,"E2"),sQuery(id+"F0.wireOp",EDGE,"E3"),sQuery(id+"F0.wireOp",EDGE,"E4"),sQuery(id+"F0.wireOp",EDGE,"E5"),sQuery(id+"F0.wireOp",EDGE,"E6"),sQuery(id+"F0.wireOp",EDGE,"E7"),sQuery(id+"F0.wireOp",EDGE,"E8"),sQuery(id+"F0.wireOp",EDGE,"E9"),sQuery(id+"F0.wireOp",EDGE,"E10"),sQuery(id+"F0.wireOp",EDGE,"E11"),sQuery(id+"F0.wireOp",EDGE,"E12"),sQuery(id+"F0.wireOp",EDGE,"E13"),sQuery(id+"F0.wireOp",EDGE,"E14"),sQuery(id+"F0.wireOp",EDGE,"E15"),sQuery(id+"F0.wireOp",EDGE,"E16"),sQuery(id+"F0.wireOp",EDGE,"E17"),sQuery(id+"F0.wireOp",EDGE,"E18"),sQuery(id+"F0.wireOp",EDGE,"E19"),sQuery(id+"F0.wireOp",EDGE,"E20"),sQuery(id+"F0.wireOp",EDGE,"E21"),sQuery(id+"F0.wireOp",EDGE,"E22"),sQuery(id+"F0.wireOp",EDGE,"E23"),sQuery(id+"F0.wireOp",EDGE,"E24"),sQuery(id+"F0.wireOp",EDGE,"E25"),sQuery(id+"F0.wireOp",EDGE,"E26"),sQuery(id+"F0.wireOp",EDGE,"E27")])],"isStart":false})});
            var sketch = newSketch(context, id + "F4", { "sketchPlane" : qUnion([Q0])});
            skLineSegment(sketch, "E711", {"start": v(6.27, 16.02) * mm, "end": v(6.3, 16) * mm});
            skLineSegment(sketch, "E712", {"start": v(6.3, 16) * mm, "end": v(6.65, 15.7) * mm});
            skLineSegment(sketch, "E713", {"start": v(6.65, 15.7) * mm, "end": v(6.68, 15.68) * mm});
            skLineSegment(sketch, "E714", {"start": v(6.68, 15.68) * mm, "end": v(6.77, 15.64) * mm});
            skLineSegment(sketch, "E715", {"start": v(6.77, 15.64) * mm, "end": v(7.47, 15.43) * mm});
            skLineSegment(sketch, "E716", {"start": v(7.47, 15.43) * mm, "end": v(7.7, 15.43) * mm});
            skLineSegment(sketch, "E717", {"start": v(7.7, 15.43) * mm, "end": v(7.86, 15.43) * mm});
            skLineSegment(sketch, "E718", {"start": v(7.86, 15.43) * mm, "end": v(8.33, 15.59) * mm});
            skLineSegment(sketch, "E719", {"start": v(8.33, 15.59) * mm, "end": v(8.56, 15.9) * mm});
            skLineSegment(sketch, "E720", {"start": v(8.56, 15.9) * mm, "end": v(8.56, 16) * mm});
            skLineSegment(sketch, "E721", {"start": v(8.56, 16) * mm, "end": v(8.56, 16.1) * mm});
            skLineSegment(sketch, "E722", {"start": v(8.56, 16.1) * mm, "end": v(8.28, 16.4) * mm});
            skLineSegment(sketch, "E723", {"start": v(8.28, 16.4) * mm, "end": v(7.69, 16.54) * mm});
            skLineSegment(sketch, "E724", {"start": v(7.69, 16.54) * mm, "end": v(7.53, 16.56) * mm});
            skLineSegment(sketch, "E725", {"start": v(7.53, 16.56) * mm, "end": v(7.33, 16.59) * mm});
            skLineSegment(sketch, "E726", {"start": v(7.33, 16.59) * mm, "end": v(6.63, 16.91) * mm});
            skLineSegment(sketch, "E727", {"start": v(6.63, 16.91) * mm, "end": v(6.32, 17.48) * mm});
            skLineSegment(sketch, "E728", {"start": v(6.32, 17.48) * mm, "end": v(6.32, 17.67) * mm});
            skLineSegment(sketch, "E729", {"start": v(6.32, 17.67) * mm, "end": v(6.32, 17.78) * mm});
            skLineSegment(sketch, "E730", {"start": v(6.32, 17.78) * mm, "end": v(6.43, 18.11) * mm});
            skLineSegment(sketch, "E731", {"start": v(6.43, 18.11) * mm, "end": v(6.74, 18.47) * mm});
            skLineSegment(sketch, "E732", {"start": v(6.74, 18.47) * mm, "end": v(7.2, 18.71) * mm});
            skLineSegment(sketch, "E733", {"start": v(7.2, 18.71) * mm, "end": v(7.66, 18.8) * mm});
            skLineSegment(sketch, "E734", {"start": v(7.66, 18.8) * mm, "end": v(7.81, 18.8) * mm});
            skLineSegment(sketch, "E735", {"start": v(7.81, 18.8) * mm, "end": v(8, 18.8) * mm});
            skLineSegment(sketch, "E736", {"start": v(8, 18.8) * mm, "end": v(8.57, 18.72) * mm});
            skLineSegment(sketch, "E737", {"start": v(8.57, 18.72) * mm, "end": v(9, 18.58) * mm});
            skLineSegment(sketch, "E738", {"start": v(9, 18.58) * mm, "end": v(9.07, 18.54) * mm});
            skLineSegment(sketch, "E739", {"start": v(9.07, 18.54) * mm, "end": v(9.07, 17.71) * mm});
            skLineSegment(sketch, "E740", {"start": v(9.07, 17.71) * mm, "end": v(9.05, 17.75) * mm});
            skLineSegment(sketch, "E741", {"start": v(9.05, 17.75) * mm, "end": v(8.65, 18.03) * mm});
            skLineSegment(sketch, "E742", {"start": v(8.65, 18.03) * mm, "end": v(8.6, 18.05) * mm});
            skLineSegment(sketch, "E743", {"start": v(8.6, 18.05) * mm, "end": v(8.53, 18.07) * mm});
            skLineSegment(sketch, "E744", {"start": v(8.53, 18.07) * mm, "end": v(8, 18.18) * mm});
            skLineSegment(sketch, "E745", {"start": v(8, 18.18) * mm, "end": v(7.81, 18.18) * mm});
            skLineSegment(sketch, "E746", {"start": v(7.81, 18.18) * mm, "end": v(7.68, 18.18) * mm});
            skLineSegment(sketch, "E747", {"start": v(7.68, 18.18) * mm, "end": v(7.3, 18.07) * mm});
            skLineSegment(sketch, "E748", {"start": v(7.3, 18.07) * mm, "end": v(7.13, 17.86) * mm});
            skLineSegment(sketch, "E749", {"start": v(7.13, 17.86) * mm, "end": v(7.13, 17.8) * mm});
            skLineSegment(sketch, "E750", {"start": v(7.13, 17.8) * mm, "end": v(7.13, 17.7) * mm});
            skLineSegment(sketch, "E751", {"start": v(7.13, 17.7) * mm, "end": v(7.4, 17.44) * mm});
            skLineSegment(sketch, "E752", {"start": v(7.4, 17.44) * mm, "end": v(8.03, 17.28) * mm});
            skLineSegment(sketch, "E753", {"start": v(8.03, 17.28) * mm, "end": v(8.22, 17.24) * mm});
            skLineSegment(sketch, "E754", {"start": v(8.22, 17.24) * mm, "end": v(8.4, 17.2) * mm});
            skLineSegment(sketch, "E755", {"start": v(8.4, 17.2) * mm, "end": v(9.09, 16.87) * mm});
            skLineSegment(sketch, "E756", {"start": v(9.09, 16.87) * mm, "end": v(9.4, 16.28) * mm});
            skLineSegment(sketch, "E757", {"start": v(9.4, 16.28) * mm, "end": v(9.39, 16.11) * mm});
            skLineSegment(sketch, "E758", {"start": v(9.39, 16.11) * mm, "end": v(9.39, 15.98) * mm});
            skLineSegment(sketch, "E759", {"start": v(9.39, 15.98) * mm, "end": v(9.27, 15.59) * mm});
            skLineSegment(sketch, "E760", {"start": v(9.27, 15.59) * mm, "end": v(8.94, 15.18) * mm});
            skLineSegment(sketch, "E761", {"start": v(8.94, 15.18) * mm, "end": v(8.41, 14.92) * mm});
            skLineSegment(sketch, "E762", {"start": v(8.41, 14.92) * mm, "end": v(7.88, 14.83) * mm});
            skLineSegment(sketch, "E763", {"start": v(7.88, 14.83) * mm, "end": v(7.7, 14.83) * mm});
            skLineSegment(sketch, "E764", {"start": v(7.7, 14.83) * mm, "end": v(7.51, 14.83) * mm});
            skLineSegment(sketch, "E765", {"start": v(7.51, 14.83) * mm, "end": v(6.95, 14.9) * mm});
            skLineSegment(sketch, "E766", {"start": v(6.95, 14.9) * mm, "end": v(6.36, 15.06) * mm});
            skLineSegment(sketch, "E767", {"start": v(6.36, 15.06) * mm, "end": v(6.27, 15.1) * mm});
            skLineSegment(sketch, "E768", {"start": v(6.27, 15.1) * mm, "end": v(6.27, 16.02) * mm});
            skLineSegment(sketch, "E769", {"start": v(-6.42, 15.85) * mm, "end": v(-6.47, 15.94) * mm});
            skLineSegment(sketch, "E770", {"start": v(-6.47, 15.94) * mm, "end": v(-6.7, 16.33) * mm});
            skLineSegment(sketch, "E771", {"start": v(-6.7, 16.33) * mm, "end": v(-6.97, 16.59) * mm});
            skLineSegment(sketch, "E772", {"start": v(-6.97, 16.59) * mm, "end": v(-7.04, 16.62) * mm});
            skLineSegment(sketch, "E773", {"start": v(-7.04, 16.62) * mm, "end": v(-6.9, 16.65) * mm});
            skLineSegment(sketch, "E774", {"start": v(-6.9, 16.65) * mm, "end": v(-6.37, 16.97) * mm});
            skLineSegment(sketch, "E775", {"start": v(-6.37, 16.97) * mm, "end": v(-6.14, 17.45) * mm});
            skLineSegment(sketch, "E776", {"start": v(-6.14, 17.45) * mm, "end": v(-6.14, 17.6) * mm});
            skLineSegment(sketch, "E777", {"start": v(-6.14, 17.6) * mm, "end": v(-6.14, 17.76) * mm});
            skLineSegment(sketch, "E778", {"start": v(-6.14, 17.76) * mm, "end": v(-6.3, 18.24) * mm});
            skLineSegment(sketch, "E779", {"start": v(-6.3, 18.24) * mm, "end": v(-6.66, 18.59) * mm});
            skLineSegment(sketch, "E780", {"start": v(-6.66, 18.59) * mm, "end": v(-6.76, 18.63) * mm});
            skLineSegment(sketch, "E781", {"start": v(-6.76, 18.63) * mm, "end": v(-6.83, 18.65) * mm});
            skLineSegment(sketch, "E782", {"start": v(-6.83, 18.65) * mm, "end": v(-7.2, 18.72) * mm});
            skLineSegment(sketch, "E783", {"start": v(-7.2, 18.72) * mm, "end": v(-7.68, 18.73) * mm});
            skLineSegment(sketch, "E784", {"start": v(-7.68, 18.73) * mm, "end": v(-7.83, 18.73) * mm});
            skLineSegment(sketch, "E785", {"start": v(-7.83, 18.73) * mm, "end": v(-9.8, 18.73) * mm});
            skLineSegment(sketch, "E786", {"start": v(-9.8, 18.73) * mm, "end": v(-9.75, 18.7) * mm});
            skLineSegment(sketch, "E787", {"start": v(-9.75, 18.7) * mm, "end": v(-9.57, 18.39) * mm});
            skLineSegment(sketch, "E788", {"start": v(-9.57, 18.39) * mm, "end": v(-9.5, 18) * mm});
            skLineSegment(sketch, "E789", {"start": v(-9.5, 18) * mm, "end": v(-9.5, 17.88) * mm});
            skLineSegment(sketch, "E790", {"start": v(-9.5, 17.88) * mm, "end": v(-9.5, 15.72) * mm});
            skLineSegment(sketch, "E791", {"start": v(-9.5, 15.72) * mm, "end": v(-9.5, 15.6) * mm});
            skLineSegment(sketch, "E792", {"start": v(-9.5, 15.6) * mm, "end": v(-9.57, 15.23) * mm});
            skLineSegment(sketch, "E793", {"start": v(-9.57, 15.23) * mm, "end": v(-9.75, 14.92) * mm});
            skLineSegment(sketch, "E794", {"start": v(-9.75, 14.92) * mm, "end": v(-9.8, 14.9) * mm});
            skLineSegment(sketch, "E795", {"start": v(-9.8, 14.9) * mm, "end": v(-8.38, 14.9) * mm});
            skLineSegment(sketch, "E796", {"start": v(-8.38, 14.9) * mm, "end": v(-8.43, 14.92) * mm});
            skLineSegment(sketch, "E797", {"start": v(-8.43, 14.92) * mm, "end": v(-8.6, 15.23) * mm});
            skLineSegment(sketch, "E798", {"start": v(-8.6, 15.23) * mm, "end": v(-8.68, 15.6) * mm});
            skLineSegment(sketch, "E799", {"start": v(-8.68, 15.6) * mm, "end": v(-8.68, 15.72) * mm});
            skLineSegment(sketch, "E800", {"start": v(-8.68, 15.72) * mm, "end": v(-8.68, 16.4) * mm});
            skLineSegment(sketch, "E801", {"start": v(-8.68, 16.4) * mm, "end": v(-8.09, 16.4) * mm});
            skLineSegment(sketch, "E802", {"start": v(-8.09, 16.4) * mm, "end": v(-8, 16.4) * mm});
            skLineSegment(sketch, "E803", {"start": v(-8, 16.4) * mm, "end": v(-7.72, 16.33) * mm});
            skLineSegment(sketch, "E804", {"start": v(-7.72, 16.33) * mm, "end": v(-7.52, 16.13) * mm});
            skLineSegment(sketch, "E805", {"start": v(-7.52, 16.13) * mm, "end": v(-7.49, 16.07) * mm});
            skLineSegment(sketch, "E806", {"start": v(-7.49, 16.07) * mm, "end": v(-7.44, 15.98) * mm});
            skLineSegment(sketch, "E807", {"start": v(-7.44, 15.98) * mm, "end": v(-6.93, 14.98) * mm});
            skLineSegment(sketch, "E808", {"start": v(-6.93, 14.98) * mm, "end": v(-6.87, 14.9) * mm});
            skLineSegment(sketch, "E809", {"start": v(-6.87, 14.9) * mm, "end": v(-5.74, 14.9) * mm});
            skLineSegment(sketch, "E810", {"start": v(-5.74, 14.9) * mm, "end": v(-5.82, 14.95) * mm});
            skLineSegment(sketch, "E811", {"start": v(-5.82, 14.95) * mm, "end": v(-6.15, 15.33) * mm});
            skLineSegment(sketch, "E812", {"start": v(-6.15, 15.33) * mm, "end": v(-6.38, 15.76) * mm});
            skLineSegment(sketch, "E813", {"start": v(-6.38, 15.76) * mm, "end": v(-6.42, 15.85) * mm});
            skLineSegment(sketch, "E814", {"start": v(-6.98, 17.56) * mm, "end": v(-6.98, 17.46) * mm});
            skLineSegment(sketch, "E815", {"start": v(-6.98, 17.46) * mm, "end": v(-7.2, 17.15) * mm});
            skLineSegment(sketch, "E816", {"start": v(-7.2, 17.15) * mm, "end": v(-7.64, 17.03) * mm});
            skLineSegment(sketch, "E817", {"start": v(-7.64, 17.03) * mm, "end": v(-7.79, 17.03) * mm});
            skLineSegment(sketch, "E818", {"start": v(-7.79, 17.03) * mm, "end": v(-8.68, 17.03) * mm});
            skLineSegment(sketch, "E819", {"start": v(-8.68, 17.03) * mm, "end": v(-8.68, 18.12) * mm});
            skLineSegment(sketch, "E820", {"start": v(-8.68, 18.12) * mm, "end": v(-7.79, 18.12) * mm});
            skLineSegment(sketch, "E821", {"start": v(-7.79, 18.12) * mm, "end": v(-7.64, 18.12) * mm});
            skLineSegment(sketch, "E822", {"start": v(-7.64, 18.12) * mm, "end": v(-7.2, 17.99) * mm});
            skLineSegment(sketch, "E823", {"start": v(-7.2, 17.99) * mm, "end": v(-6.98, 17.67) * mm});
            skLineSegment(sketch, "E824", {"start": v(-6.98, 17.67) * mm, "end": v(-6.98, 17.56) * mm});
            skLineSegment(sketch, "E825", {"start": v(-4.25, 15.79) * mm, "end": v(-4.3, 15.84) * mm});
            skLineSegment(sketch, "E826", {"start": v(-4.3, 15.84) * mm, "end": v(-4.5, 16.2) * mm});
            skLineSegment(sketch, "E827", {"start": v(-4.5, 16.2) * mm, "end": v(-4.59, 16.66) * mm});
            skLineSegment(sketch, "E828", {"start": v(-4.59, 16.66) * mm, "end": v(-4.59, 16.81) * mm});
            skLineSegment(sketch, "E829", {"start": v(-4.59, 16.81) * mm, "end": v(-4.59, 16.96) * mm});
            skLineSegment(sketch, "E830", {"start": v(-4.59, 16.96) * mm, "end": v(-4.5, 17.4) * mm});
            skLineSegment(sketch, "E831", {"start": v(-4.5, 17.4) * mm, "end": v(-4.3, 17.78) * mm});
            skLineSegment(sketch, "E832", {"start": v(-4.3, 17.78) * mm, "end": v(-4.25, 17.84) * mm});
            skLineSegment(sketch, "E833", {"start": v(-4.25, 17.84) * mm, "end": v(-4.2, 17.89) * mm});
            skLineSegment(sketch, "E834", {"start": v(-4.2, 17.89) * mm, "end": v(-3.63, 18.16) * mm});
            skLineSegment(sketch, "E835", {"start": v(-3.63, 18.16) * mm, "end": v(-3.43, 18.16) * mm});
            skLineSegment(sketch, "E836", {"start": v(-3.43, 18.16) * mm, "end": v(-3.23, 18.16) * mm});
            skLineSegment(sketch, "E837", {"start": v(-3.23, 18.16) * mm, "end": v(-2.67, 17.89) * mm});
            skLineSegment(sketch, "E838", {"start": v(-2.67, 17.89) * mm, "end": v(-2.62, 17.84) * mm});
            skLineSegment(sketch, "E839", {"start": v(-2.62, 17.84) * mm, "end": v(-2.57, 17.78) * mm});
            skLineSegment(sketch, "E840", {"start": v(-2.57, 17.78) * mm, "end": v(-2.36, 17.4) * mm});
            skLineSegment(sketch, "E841", {"start": v(-2.36, 17.4) * mm, "end": v(-2.26, 16.96) * mm});
            skLineSegment(sketch, "E842", {"start": v(-2.26, 16.96) * mm, "end": v(-2.26, 16.81) * mm});
            skLineSegment(sketch, "E843", {"start": v(-2.26, 16.81) * mm, "end": v(-2.26, 16.66) * mm});
            skLineSegment(sketch, "E844", {"start": v(-2.26, 16.66) * mm, "end": v(-2.36, 16.2) * mm});
            skLineSegment(sketch, "E845", {"start": v(-2.36, 16.2) * mm, "end": v(-2.57, 15.84) * mm});
            skLineSegment(sketch, "E846", {"start": v(-2.57, 15.84) * mm, "end": v(-2.62, 15.79) * mm});
            skLineSegment(sketch, "E847", {"start": v(-2.62, 15.79) * mm, "end": v(-2.67, 15.74) * mm});
            skLineSegment(sketch, "E848", {"start": v(-2.67, 15.74) * mm, "end": v(-3.24, 15.47) * mm});
            skLineSegment(sketch, "E849", {"start": v(-3.24, 15.47) * mm, "end": v(-3.43, 15.47) * mm});
            skLineSegment(sketch, "E850", {"start": v(-3.43, 15.47) * mm, "end": v(-3.64, 15.47) * mm});
            skLineSegment(sketch, "E851", {"start": v(-3.64, 15.47) * mm, "end": v(-4.2, 15.74) * mm});
            skLineSegment(sketch, "E852", {"start": v(-4.2, 15.74) * mm, "end": v(-4.25, 15.79) * mm});
            skLineSegment(sketch, "E853", {"start": v(-3.43, 14.79) * mm, "end": v(-3.25, 14.79) * mm});
            skLineSegment(sketch, "E854", {"start": v(-3.25, 14.79) * mm, "end": v(-2.7, 14.9) * mm});
            skLineSegment(sketch, "E855", {"start": v(-2.7, 14.9) * mm, "end": v(-2.2, 15.16) * mm});
            skLineSegment(sketch, "E856", {"start": v(-2.2, 15.16) * mm, "end": v(-2.11, 15.23) * mm});
            skLineSegment(sketch, "E857", {"start": v(-2.11, 15.23) * mm, "end": v(-2.01, 15.32) * mm});
            skLineSegment(sketch, "E858", {"start": v(-2.01, 15.32) * mm, "end": v(-1.62, 15.88) * mm});
            skLineSegment(sketch, "E859", {"start": v(-1.62, 15.88) * mm, "end": v(-1.43, 16.58) * mm});
            skLineSegment(sketch, "E860", {"start": v(-1.43, 16.58) * mm, "end": v(-1.43, 16.81) * mm});
            skLineSegment(sketch, "E861", {"start": v(-1.43, 16.81) * mm, "end": v(-1.43, 17.04) * mm});
            skLineSegment(sketch, "E862", {"start": v(-1.43, 17.04) * mm, "end": v(-1.62, 17.74) * mm});
            skLineSegment(sketch, "E863", {"start": v(-1.62, 17.74) * mm, "end": v(-2.01, 18.3) * mm});
            skLineSegment(sketch, "E864", {"start": v(-2.01, 18.3) * mm, "end": v(-2.11, 18.4) * mm});
            skLineSegment(sketch, "E865", {"start": v(-2.11, 18.4) * mm, "end": v(-2.2, 18.46) * mm});
            skLineSegment(sketch, "E866", {"start": v(-2.2, 18.46) * mm, "end": v(-2.7, 18.71) * mm});
            skLineSegment(sketch, "E867", {"start": v(-2.7, 18.71) * mm, "end": v(-3.25, 18.82) * mm});
            skLineSegment(sketch, "E868", {"start": v(-3.25, 18.82) * mm, "end": v(-3.43, 18.82) * mm});
            skLineSegment(sketch, "E869", {"start": v(-3.43, 18.82) * mm, "end": v(-3.62, 18.82) * mm});
            skLineSegment(sketch, "E870", {"start": v(-3.62, 18.82) * mm, "end": v(-4.17, 18.71) * mm});
            skLineSegment(sketch, "E871", {"start": v(-4.17, 18.71) * mm, "end": v(-4.67, 18.46) * mm});
            skLineSegment(sketch, "E872", {"start": v(-4.67, 18.46) * mm, "end": v(-4.76, 18.4) * mm});
            skLineSegment(sketch, "E873", {"start": v(-4.76, 18.4) * mm, "end": v(-4.86, 18.3) * mm});
            skLineSegment(sketch, "E874", {"start": v(-4.86, 18.3) * mm, "end": v(-5.25, 17.74) * mm});
            skLineSegment(sketch, "E875", {"start": v(-5.25, 17.74) * mm, "end": v(-5.44, 17.04) * mm});
            skLineSegment(sketch, "E876", {"start": v(-5.44, 17.04) * mm, "end": v(-5.44, 16.81) * mm});
            skLineSegment(sketch, "E877", {"start": v(-5.44, 16.81) * mm, "end": v(-5.44, 16.58) * mm});
            skLineSegment(sketch, "E878", {"start": v(-5.44, 16.58) * mm, "end": v(-5.25, 15.88) * mm});
            skLineSegment(sketch, "E879", {"start": v(-5.25, 15.88) * mm, "end": v(-4.86, 15.32) * mm});
            skLineSegment(sketch, "E880", {"start": v(-4.86, 15.32) * mm, "end": v(-4.76, 15.23) * mm});
            skLineSegment(sketch, "E881", {"start": v(-4.76, 15.23) * mm, "end": v(-4.67, 15.16) * mm});
            skLineSegment(sketch, "E882", {"start": v(-4.67, 15.16) * mm, "end": v(-4.16, 14.9) * mm});
            skLineSegment(sketch, "E883", {"start": v(-4.16, 14.9) * mm, "end": v(-3.62, 14.79) * mm});
            skLineSegment(sketch, "E884", {"start": v(-3.62, 14.79) * mm, "end": v(-3.43, 14.79) * mm});
            skLineSegment(sketch, "E885", {"start": v(2.11, 15.87) * mm, "end": v(2.06, 15.8) * mm});
            skLineSegment(sketch, "E886", {"start": v(2.06, 15.8) * mm, "end": v(1.64, 15.59) * mm});
            skLineSegment(sketch, "E887", {"start": v(1.64, 15.59) * mm, "end": v(1.13, 15.51) * mm});
            skLineSegment(sketch, "E888", {"start": v(1.13, 15.51) * mm, "end": v(0.96, 15.51) * mm});
            skLineSegment(sketch, "E889", {"start": v(0.96, 15.51) * mm, "end": v(0.21, 15.51) * mm});
            skLineSegment(sketch, "E890", {"start": v(0.21, 15.51) * mm, "end": v(0.21, 17.88) * mm});
            skLineSegment(sketch, "E891", {"start": v(0.21, 17.88) * mm, "end": v(0.21, 18) * mm});
            skLineSegment(sketch, "E892", {"start": v(0.21, 18) * mm, "end": v(0.29, 18.38) * mm});
            skLineSegment(sketch, "E893", {"start": v(0.29, 18.38) * mm, "end": v(0.45, 18.7) * mm});
            skLineSegment(sketch, "E894", {"start": v(0.45, 18.7) * mm, "end": v(0.5, 18.73) * mm});
            skLineSegment(sketch, "E895", {"start": v(0.5, 18.73) * mm, "end": v(-0.9, 18.73) * mm});
            skLineSegment(sketch, "E896", {"start": v(-0.9, 18.73) * mm, "end": v(-0.85, 18.7) * mm});
            skLineSegment(sketch, "E897", {"start": v(-0.85, 18.7) * mm, "end": v(-0.67, 18.38) * mm});
            skLineSegment(sketch, "E898", {"start": v(-0.67, 18.38) * mm, "end": v(-0.6, 18) * mm});
            skLineSegment(sketch, "E899", {"start": v(-0.6, 18) * mm, "end": v(-0.6, 17.88) * mm});
            skLineSegment(sketch, "E900", {"start": v(-0.6, 17.88) * mm, "end": v(-0.6, 15.72) * mm});
            skLineSegment(sketch, "E901", {"start": v(-0.6, 15.72) * mm, "end": v(-0.6, 15.6) * mm});
            skLineSegment(sketch, "E902", {"start": v(-0.6, 15.6) * mm, "end": v(-0.67, 15.23) * mm});
            skLineSegment(sketch, "E903", {"start": v(-0.67, 15.23) * mm, "end": v(-0.85, 14.93) * mm});
            skLineSegment(sketch, "E904", {"start": v(-0.85, 14.93) * mm, "end": v(-0.9, 14.9) * mm});
            skLineSegment(sketch, "E905", {"start": v(-0.9, 14.9) * mm, "end": v(1.99, 14.9) * mm});
            skLineSegment(sketch, "E906", {"start": v(1.99, 14.9) * mm, "end": v(2.11, 15.87) * mm});
            skLineSegment(sketch, "E907", {"start": v(5.6, 15.87) * mm, "end": v(5.54, 15.8) * mm});
            skLineSegment(sketch, "E908", {"start": v(5.54, 15.8) * mm, "end": v(5.12, 15.58) * mm});
            skLineSegment(sketch, "E909", {"start": v(5.12, 15.58) * mm, "end": v(4.56, 15.5) * mm});
            skLineSegment(sketch, "E910", {"start": v(4.56, 15.5) * mm, "end": v(4.44, 15.51) * mm});
            skLineSegment(sketch, "E911", {"start": v(4.44, 15.51) * mm, "end": v(3.67, 15.51) * mm});
            skLineSegment(sketch, "E912", {"start": v(3.67, 15.51) * mm, "end": v(3.67, 17.88) * mm});
            skLineSegment(sketch, "E913", {"start": v(3.67, 17.88) * mm, "end": v(3.67, 18) * mm});
            skLineSegment(sketch, "E914", {"start": v(3.67, 18) * mm, "end": v(3.75, 18.38) * mm});
            skLineSegment(sketch, "E915", {"start": v(3.75, 18.38) * mm, "end": v(3.92, 18.7) * mm});
            skLineSegment(sketch, "E916", {"start": v(3.92, 18.7) * mm, "end": v(3.97, 18.73) * mm});
            skLineSegment(sketch, "E917", {"start": v(3.97, 18.73) * mm, "end": v(2.58, 18.73) * mm});
            skLineSegment(sketch, "E918", {"start": v(2.58, 18.73) * mm, "end": v(2.63, 18.7) * mm});
            skLineSegment(sketch, "E919", {"start": v(2.63, 18.7) * mm, "end": v(2.8, 18.38) * mm});
            skLineSegment(sketch, "E920", {"start": v(2.8, 18.38) * mm, "end": v(2.88, 18) * mm});
            skLineSegment(sketch, "E921", {"start": v(2.88, 18) * mm, "end": v(2.88, 17.88) * mm});
            skLineSegment(sketch, "E922", {"start": v(2.88, 17.88) * mm, "end": v(2.88, 15.72) * mm});
            skLineSegment(sketch, "E923", {"start": v(2.88, 15.72) * mm, "end": v(2.88, 15.6) * mm});
            skLineSegment(sketch, "E924", {"start": v(2.88, 15.6) * mm, "end": v(2.8, 15.22) * mm});
            skLineSegment(sketch, "E925", {"start": v(2.8, 15.22) * mm, "end": v(2.63, 14.9) * mm});
            skLineSegment(sketch, "E926", {"start": v(2.63, 14.9) * mm, "end": v(2.58, 14.87) * mm});
            skLineSegment(sketch, "E927", {"start": v(2.58, 14.87) * mm, "end": v(5.44, 14.87) * mm});
            skLineSegment(sketch, "E928", {"start": v(5.44, 14.87) * mm, "end": v(5.6, 15.87) * mm});
            skLineSegment(sketch, "E929", {"start": v(-1.8, -8.84) * mm, "end": v(-1.8, -3.1) * mm});
            skLineSegment(sketch, "E930", {"start": v(-1.8, -3.1) * mm, "end": v(-1.65, -3.09) * mm});
            skLineSegment(sketch, "E931", {"start": v(-1.65, -3.09) * mm, "end": v(-0.3, -3.02) * mm});
            skLineSegment(sketch, "E932", {"start": v(-0.3, -3.02) * mm, "end": v(-0.17, -3) * mm});
            skLineSegment(sketch, "E933", {"start": v(-0.17, -3) * mm, "end": v(-0.22, -2.9) * mm});
            skLineSegment(sketch, "E934", {"start": v(-0.22, -2.9) * mm, "end": v(-0.73, -1.8) * mm});
            skLineSegment(sketch, "E935", {"start": v(-0.73, -1.8) * mm, "end": v(-0.79, -1.69) * mm});
            skLineSegment(sketch, "E936", {"start": v(-0.79, -1.69) * mm, "end": v(-0.87, -1.7) * mm});
            skLineSegment(sketch, "E937", {"start": v(-0.87, -1.7) * mm, "end": v(-1.7, -1.75) * mm});
            skLineSegment(sketch, "E938", {"start": v(-1.7, -1.75) * mm, "end": v(-1.8, -1.75) * mm});
            skLineSegment(sketch, "E939", {"start": v(-1.8, -1.75) * mm, "end": v(-1.8, -0.56) * mm});
            skLineSegment(sketch, "E940", {"start": v(-1.8, -0.56) * mm, "end": v(-1.98, -0.6) * mm});
            skLineSegment(sketch, "E941", {"start": v(-1.98, -0.6) * mm, "end": v(-3.97, -0.92) * mm});
            skLineSegment(sketch, "E942", {"start": v(-3.97, -0.92) * mm, "end": v(-4.18, -0.94) * mm});
            skLineSegment(sketch, "E943", {"start": v(-4.18, -0.94) * mm, "end": v(-4.18, -8.84) * mm});
            skLineSegment(sketch, "E944", {"start": v(-4.18, -8.84) * mm, "end": v(-4.18, -9.1) * mm});
            skLineSegment(sketch, "E945", {"start": v(-4.18, -9.1) * mm, "end": v(-4.32, -9.92) * mm});
            skLineSegment(sketch, "E946", {"start": v(-4.32, -9.92) * mm, "end": v(-4.65, -10.64) * mm});
            skLineSegment(sketch, "E947", {"start": v(-4.65, -10.64) * mm, "end": v(-5.07, -11.09) * mm});
            skLineSegment(sketch, "E948", {"start": v(-5.07, -11.09) * mm, "end": v(-5.38, -11.3) * mm});
            skLineSegment(sketch, "E949", {"start": v(-5.38, -11.3) * mm, "end": v(-5.48, -11.37) * mm});
            skLineSegment(sketch, "E950", {"start": v(-5.48, -11.37) * mm, "end": v(-0.49, -11.37) * mm});
            skLineSegment(sketch, "E951", {"start": v(-0.49, -11.37) * mm, "end": v(-0.6, -11.3) * mm});
            skLineSegment(sketch, "E952", {"start": v(-0.6, -11.3) * mm, "end": v(-0.9, -11.09) * mm});
            skLineSegment(sketch, "E953", {"start": v(-0.9, -11.09) * mm, "end": v(-1.32, -10.64) * mm});
            skLineSegment(sketch, "E954", {"start": v(-1.32, -10.64) * mm, "end": v(-1.65, -9.92) * mm});
            skLineSegment(sketch, "E955", {"start": v(-1.65, -9.92) * mm, "end": v(-1.8, -9.1) * mm});
            skLineSegment(sketch, "E956", {"start": v(-1.8, -9.1) * mm, "end": v(-1.8, -8.84) * mm});
            skLineSegment(sketch, "E957", {"start": v(9.82, -11.35) * mm, "end": v(9.71, -11.25) * mm});
            skLineSegment(sketch, "E958", {"start": v(9.71, -11.25) * mm, "end": v(9.17, -10.57) * mm});
            skLineSegment(sketch, "E959", {"start": v(9.17, -10.57) * mm, "end": v(8.7, -9.49) * mm});
            skLineSegment(sketch, "E960", {"start": v(8.7, -9.49) * mm, "end": v(8.64, -9.2) * mm});
            skLineSegment(sketch, "E961", {"start": v(8.64, -9.2) * mm, "end": v(8.54, -8.75) * mm});
            skLineSegment(sketch, "E962", {"start": v(8.54, -8.75) * mm, "end": v(8.18, -7.43) * mm});
            skLineSegment(sketch, "E963", {"start": v(8.18, -7.43) * mm, "end": v(7.48, -5.48) * mm});
            skLineSegment(sketch, "E964", {"start": v(7.48, -5.48) * mm, "end": v(6.48, -3.5) * mm});
            skLineSegment(sketch, "E965", {"start": v(6.48, -3.5) * mm, "end": v(5.5, -2.07) * mm});
            skLineSegment(sketch, "E966", {"start": v(5.5, -2.07) * mm, "end": v(5.12, -1.64) * mm});
            skLineSegment(sketch, "E967", {"start": v(5.12, -1.64) * mm, "end": v(5.48, -1.44) * mm});
            skLineSegment(sketch, "E968", {"start": v(5.48, -1.44) * mm, "end": v(6.49, -0.7) * mm});
            skLineSegment(sketch, "E969", {"start": v(6.49, -0.7) * mm, "end": v(7.51, 0.47) * mm});
            skLineSegment(sketch, "E970", {"start": v(7.51, 0.47) * mm, "end": v(8.16, 1.83) * mm});
            skLineSegment(sketch, "E971", {"start": v(8.16, 1.83) * mm, "end": v(8.39, 2.99) * mm});
            skLineSegment(sketch, "E972", {"start": v(8.39, 2.99) * mm, "end": v(8.39, 3.37) * mm});
            skLineSegment(sketch, "E973", {"start": v(8.39, 3.37) * mm, "end": v(8.39, 3.66) * mm});
            skLineSegment(sketch, "E974", {"start": v(8.39, 3.66) * mm, "end": v(8.25, 4.53) * mm});
            skLineSegment(sketch, "E975", {"start": v(8.25, 4.53) * mm, "end": v(7.83, 5.65) * mm});
            skLineSegment(sketch, "E976", {"start": v(7.83, 5.65) * mm, "end": v(7.15, 6.66) * mm});
            skLineSegment(sketch, "E977", {"start": v(7.15, 6.66) * mm, "end": v(6.47, 7.31) * mm});
            skLineSegment(sketch, "E978", {"start": v(6.47, 7.31) * mm, "end": v(6.21, 7.49) * mm});
            skLineSegment(sketch, "E979", {"start": v(6.21, 7.49) * mm, "end": v(6.06, 7.59) * mm});
            skLineSegment(sketch, "E980", {"start": v(6.06, 7.59) * mm, "end": v(5.23, 7.99) * mm});
            skLineSegment(sketch, "E981", {"start": v(5.23, 7.99) * mm, "end": v(4.28, 8.28) * mm});
            skLineSegment(sketch, "E982", {"start": v(4.28, 8.28) * mm, "end": v(4.08, 8.32) * mm});
            skLineSegment(sketch, "E983", {"start": v(4.08, 8.32) * mm, "end": v(4.15, 8.16) * mm});
            skLineSegment(sketch, "E984", {"start": v(4.15, 8.16) * mm, "end": v(4.6, 6.49) * mm});
            skLineSegment(sketch, "E985", {"start": v(4.6, 6.49) * mm, "end": v(4.61, 6.31) * mm});
            skLineSegment(sketch, "E986", {"start": v(4.61, 6.31) * mm, "end": v(4.83, 6.14) * mm});
            skLineSegment(sketch, "E987", {"start": v(4.83, 6.14) * mm, "end": v(5.6, 5.04) * mm});
            skLineSegment(sketch, "E988", {"start": v(5.6, 5.04) * mm, "end": v(5.95, 3.76) * mm});
            skLineSegment(sketch, "E989", {"start": v(5.95, 3.76) * mm, "end": v(5.95, 3.33) * mm});
            skLineSegment(sketch, "E990", {"start": v(5.95, 3.33) * mm, "end": v(5.95, 3.02) * mm});
            skLineSegment(sketch, "E991", {"start": v(5.95, 3.02) * mm, "end": v(5.78, 2.1) * mm});
            skLineSegment(sketch, "E992", {"start": v(5.78, 2.1) * mm, "end": v(5.2, 0.87) * mm});
            skLineSegment(sketch, "E993", {"start": v(5.2, 0.87) * mm, "end": v(4.07, -0.23) * mm});
            skLineSegment(sketch, "E994", {"start": v(4.07, -0.23) * mm, "end": v(2.77, -0.95) * mm});
            skLineSegment(sketch, "E995", {"start": v(2.77, -0.95) * mm, "end": v(2.3, -1.1) * mm});
            skLineSegment(sketch, "E996", {"start": v(2.3, -1.1) * mm, "end": v(2.36, -1.22) * mm});
            skLineSegment(sketch, "E997", {"start": v(2.36, -1.22) * mm, "end": v(2.92, -2.36) * mm});
            skLineSegment(sketch, "E998", {"start": v(2.92, -2.36) * mm, "end": v(2.97, -2.48) * mm});
            skLineSegment(sketch, "E999", {"start": v(2.97, -2.48) * mm, "end": v(3, -2.47) * mm});
            skLineSegment(sketch, "E1000", {"start": v(3, -2.47) * mm, "end": v(3.38, -2.36) * mm});
            skLineSegment(sketch, "E1001", {"start": v(3.38, -2.36) * mm, "end": v(3.42, -2.35) * mm});
            skLineSegment(sketch, "E1002", {"start": v(3.42, -2.35) * mm, "end": v(3.74, -2.73) * mm});
            skLineSegment(sketch, "E1003", {"start": v(3.74, -2.73) * mm, "end": v(5.14, -5.18) * mm});
            skLineSegment(sketch, "E1004", {"start": v(5.14, -5.18) * mm, "end": v(6.04, -7.97) * mm});
            skLineSegment(sketch, "E1005", {"start": v(6.04, -7.97) * mm, "end": v(6.12, -8.53) * mm});
            skLineSegment(sketch, "E1006", {"start": v(6.12, -8.53) * mm, "end": v(6.16, -8.8) * mm});
            skLineSegment(sketch, "E1007", {"start": v(6.16, -8.8) * mm, "end": v(6.16, -9.6) * mm});
            skLineSegment(sketch, "E1008", {"start": v(6.16, -9.6) * mm, "end": v(6, -10.4) * mm});
            skLineSegment(sketch, "E1009", {"start": v(6, -10.4) * mm, "end": v(5.7, -10.98) * mm});
            skLineSegment(sketch, "E1010", {"start": v(5.7, -10.98) * mm, "end": v(5.48, -11.26) * mm});
            skLineSegment(sketch, "E1011", {"start": v(5.48, -11.26) * mm, "end": v(5.4, -11.35) * mm});
            skLineSegment(sketch, "E1012", {"start": v(5.4, -11.35) * mm, "end": v(9.82, -11.35) * mm});
            skLineSegment(sketch, "E1013", {"start": v(4.84, -8.77) * mm, "end": v(4.74, -8.67) * mm});
            skLineSegment(sketch, "E1014", {"start": v(4.74, -8.67) * mm, "end": v(4.19, -7.99) * mm});
            skLineSegment(sketch, "E1015", {"start": v(4.19, -7.99) * mm, "end": v(3.73, -6.9) * mm});
            skLineSegment(sketch, "E1016", {"start": v(3.73, -6.9) * mm, "end": v(3.67, -6.62) * mm});
            skLineSegment(sketch, "E1017", {"start": v(3.67, -6.62) * mm, "end": v(3.55, -6.08) * mm});
            skLineSegment(sketch, "E1018", {"start": v(3.55, -6.08) * mm, "end": v(2.56, -2.94) * mm});
            skLineSegment(sketch, "E1019", {"start": v(2.56, -2.94) * mm, "end": v(0.85, 0.19) * mm});
            skLineSegment(sketch, "E1020", {"start": v(0.85, 0.19) * mm, "end": v(0.39, 0.73) * mm});
            skLineSegment(sketch, "E1021", {"start": v(0.39, 0.73) * mm, "end": v(0.4, 0.74) * mm});
            skLineSegment(sketch, "E1022", {"start": v(0.4, 0.74) * mm, "end": v(0.6, 0.82) * mm});
            skLineSegment(sketch, "E1023", {"start": v(0.6, 0.82) * mm, "end": v(0.62, 0.83) * mm});
            skLineSegment(sketch, "E1024", {"start": v(0.62, 0.83) * mm, "end": v(1, 1.03) * mm});
            skLineSegment(sketch, "E1025", {"start": v(1, 1.03) * mm, "end": v(2.06, 1.78) * mm});
            skLineSegment(sketch, "E1026", {"start": v(2.06, 1.78) * mm, "end": v(3.14, 2.97) * mm});
            skLineSegment(sketch, "E1027", {"start": v(3.14, 2.97) * mm, "end": v(3.82, 4.37) * mm});
            skLineSegment(sketch, "E1028", {"start": v(3.82, 4.37) * mm, "end": v(4.05, 5.56) * mm});
            skLineSegment(sketch, "E1029", {"start": v(4.05, 5.56) * mm, "end": v(4.05, 5.95) * mm});
            skLineSegment(sketch, "E1030", {"start": v(4.05, 5.95) * mm, "end": v(4.06, 6.24) * mm});
            skLineSegment(sketch, "E1031", {"start": v(4.06, 6.24) * mm, "end": v(3.92, 7.12) * mm});
            skLineSegment(sketch, "E1032", {"start": v(3.92, 7.12) * mm, "end": v(3.5, 8.24) * mm});
            skLineSegment(sketch, "E1033", {"start": v(3.5, 8.24) * mm, "end": v(2.81, 9.24) * mm});
            skLineSegment(sketch, "E1034", {"start": v(2.81, 9.24) * mm, "end": v(2.13, 9.9) * mm});
            skLineSegment(sketch, "E1035", {"start": v(2.13, 9.9) * mm, "end": v(1.88, 10.07) * mm});
            skLineSegment(sketch, "E1036", {"start": v(1.88, 10.07) * mm, "end": v(1.6, 10.26) * mm});
            skLineSegment(sketch, "E1037", {"start": v(1.6, 10.26) * mm, "end": v(-0.08, 10.87) * mm});
            skLineSegment(sketch, "E1038", {"start": v(-0.08, 10.87) * mm, "end": v(-1.99, 11.12) * mm});
            skLineSegment(sketch, "E1039", {"start": v(-1.99, 11.12) * mm, "end": v(-2.62, 11.12) * mm});
            skLineSegment(sketch, "E1040", {"start": v(-2.62, 11.12) * mm, "end": v(-9.82, 11.12) * mm});
            skLineSegment(sketch, "E1041", {"start": v(-9.82, 11.12) * mm, "end": v(-9.71, 11.05) * mm});
            skLineSegment(sketch, "E1042", {"start": v(-9.71, 11.05) * mm, "end": v(-9.4, 10.83) * mm});
            skLineSegment(sketch, "E1043", {"start": v(-9.4, 10.83) * mm, "end": v(-8.98, 10.38) * mm});
            skLineSegment(sketch, "E1044", {"start": v(-8.98, 10.38) * mm, "end": v(-8.65, 9.67) * mm});
            skLineSegment(sketch, "E1045", {"start": v(-8.65, 9.67) * mm, "end": v(-8.51, 8.85) * mm});
            skLineSegment(sketch, "E1046", {"start": v(-8.51, 8.85) * mm, "end": v(-8.51, 8.58) * mm});
            skLineSegment(sketch, "E1047", {"start": v(-8.51, 8.58) * mm, "end": v(-8.51, -6.23) * mm});
            skLineSegment(sketch, "E1048", {"start": v(-8.51, -6.23) * mm, "end": v(-8.51, -6.5) * mm});
            skLineSegment(sketch, "E1049", {"start": v(-8.51, -6.5) * mm, "end": v(-8.65, -7.33) * mm});
            skLineSegment(sketch, "E1050", {"start": v(-8.65, -7.33) * mm, "end": v(-8.98, -8.04) * mm});
            skLineSegment(sketch, "E1051", {"start": v(-8.98, -8.04) * mm, "end": v(-9.4, -8.49) * mm});
            skLineSegment(sketch, "E1052", {"start": v(-9.4, -8.49) * mm, "end": v(-9.71, -8.7) * mm});
            skLineSegment(sketch, "E1053", {"start": v(-9.71, -8.7) * mm, "end": v(-9.82, -8.77) * mm});
            skLineSegment(sketch, "E1054", {"start": v(-9.82, -8.77) * mm, "end": v(-4.82, -8.77) * mm});
            skLineSegment(sketch, "E1055", {"start": v(-4.82, -8.77) * mm, "end": v(-4.92, -8.7) * mm});
            skLineSegment(sketch, "E1056", {"start": v(-4.92, -8.7) * mm, "end": v(-5.22, -8.49) * mm});
            skLineSegment(sketch, "E1057", {"start": v(-5.22, -8.49) * mm, "end": v(-5.65, -8.04) * mm});
            skLineSegment(sketch, "E1058", {"start": v(-5.65, -8.04) * mm, "end": v(-5.99, -7.33) * mm});
            skLineSegment(sketch, "E1059", {"start": v(-5.99, -7.33) * mm, "end": v(-6.12, -6.5) * mm});
            skLineSegment(sketch, "E1060", {"start": v(-6.12, -6.5) * mm, "end": v(-6.12, -6.23) * mm});
            skLineSegment(sketch, "E1061", {"start": v(-6.12, -6.23) * mm, "end": v(-6.12, -0.5) * mm});
            skLineSegment(sketch, "E1062", {"start": v(-6.12, -0.5) * mm, "end": v(-5.5, -0.5) * mm});
            skLineSegment(sketch, "E1063", {"start": v(-5.5, -0.5) * mm, "end": v(-3.6, -0.34) * mm});
            skLineSegment(sketch, "E1064", {"start": v(-3.6, -0.34) * mm, "end": v(-1.7, 0) * mm});
            skLineSegment(sketch, "E1065", {"start": v(-1.7, 0) * mm, "end": v(-1.34, 0.08) * mm});
            skLineSegment(sketch, "E1066", {"start": v(-1.34, 0.08) * mm, "end": v(-1.03, -0.3) * mm});
            skLineSegment(sketch, "E1067", {"start": v(-1.03, -0.3) * mm, "end": v(0.26, -2.68) * mm});
            skLineSegment(sketch, "E1068", {"start": v(0.26, -2.68) * mm, "end": v(1.08, -5.4) * mm});
            skLineSegment(sketch, "E1069", {"start": v(1.08, -5.4) * mm, "end": v(1.15, -5.93) * mm});
            skLineSegment(sketch, "E1070", {"start": v(1.15, -5.93) * mm, "end": v(1.19, -6.2) * mm});
            skLineSegment(sketch, "E1071", {"start": v(1.19, -6.2) * mm, "end": v(1.18, -7) * mm});
            skLineSegment(sketch, "E1072", {"start": v(1.18, -7) * mm, "end": v(1.01, -7.82) * mm});
            skLineSegment(sketch, "E1073", {"start": v(1.01, -7.82) * mm, "end": v(0.73, -8.4) * mm});
            skLineSegment(sketch, "E1074", {"start": v(0.73, -8.4) * mm, "end": v(0.51, -8.68) * mm});
            skLineSegment(sketch, "E1075", {"start": v(0.51, -8.68) * mm, "end": v(0.43, -8.77) * mm});
            skLineSegment(sketch, "E1076", {"start": v(0.43, -8.77) * mm, "end": v(4.84, -8.77) * mm});
            skLineSegment(sketch, "E1077", {"start": v(-6.12, 0.83) * mm, "end": v(-6.12, 9.8) * mm});
            skLineSegment(sketch, "E1078", {"start": v(-6.12, 9.8) * mm, "end": v(-2.73, 9.8) * mm});
            skLineSegment(sketch, "E1079", {"start": v(-2.73, 9.8) * mm, "end": v(-2.42, 9.79) * mm});
            skLineSegment(sketch, "E1080", {"start": v(-2.42, 9.79) * mm, "end": v(-1.1, 9.58) * mm});
            skLineSegment(sketch, "E1081", {"start": v(-1.1, 9.58) * mm, "end": v(-0.03, 9.13) * mm});
            skLineSegment(sketch, "E1082", {"start": v(-0.03, 9.13) * mm, "end": v(0.15, 9) * mm});
            skLineSegment(sketch, "E1083", {"start": v(0.15, 9) * mm, "end": v(0.39, 8.83) * mm});
            skLineSegment(sketch, "E1084", {"start": v(0.39, 8.83) * mm, "end": v(1.25, 7.7) * mm});
            skLineSegment(sketch, "E1085", {"start": v(1.25, 7.7) * mm, "end": v(1.62, 6.37) * mm});
            skLineSegment(sketch, "E1086", {"start": v(1.62, 6.37) * mm, "end": v(1.62, 5.93) * mm});
            skLineSegment(sketch, "E1087", {"start": v(1.62, 5.93) * mm, "end": v(1.62, 5.5) * mm});
            skLineSegment(sketch, "E1088", {"start": v(1.62, 5.5) * mm, "end": v(1.29, 4.22) * mm});
            skLineSegment(sketch, "E1089", {"start": v(1.29, 4.22) * mm, "end": v(0.08, 2.6) * mm});
            skLineSegment(sketch, "E1090", {"start": v(0.08, 2.6) * mm, "end": v(-2.29, 1.37) * mm});
            skLineSegment(sketch, "E1091", {"start": v(-2.29, 1.37) * mm, "end": v(-5.16, 0.85) * mm});
            skLineSegment(sketch, "E1092", {"start": v(-5.16, 0.85) * mm, "end": v(-6.12, 0.83) * mm});
            skLineSegment(sketch, "E1093", {"start": v(-1.8, 2.11) * mm, "end": v(-1.8, 7.17) * mm});
            skLineSegment(sketch, "E1094", {"start": v(-1.8, 7.17) * mm, "end": v(0.9, 7.17) * mm});
            skLineSegment(sketch, "E1095", {"start": v(0.9, 7.17) * mm, "end": v(0.85, 7.3) * mm});
            skLineSegment(sketch, "E1096", {"start": v(0.85, 7.3) * mm, "end": v(0.5, 7.92) * mm});
            skLineSegment(sketch, "E1097", {"start": v(0.5, 7.92) * mm, "end": v(0.01, 8.43) * mm});
            skLineSegment(sketch, "E1098", {"start": v(0.01, 8.43) * mm, "end": v(-0.1, 8.51) * mm});
            skLineSegment(sketch, "E1099", {"start": v(-0.1, 8.51) * mm, "end": v(-5.48, 8.51) * mm});
            skLineSegment(sketch, "E1100", {"start": v(-5.48, 8.51) * mm, "end": v(-5.38, 8.45) * mm});
            skLineSegment(sketch, "E1101", {"start": v(-5.38, 8.45) * mm, "end": v(-5.07, 8.23) * mm});
            skLineSegment(sketch, "E1102", {"start": v(-5.07, 8.23) * mm, "end": v(-4.65, 7.79) * mm});
            skLineSegment(sketch, "E1103", {"start": v(-4.65, 7.79) * mm, "end": v(-4.32, 7.07) * mm});
            skLineSegment(sketch, "E1104", {"start": v(-4.32, 7.07) * mm, "end": v(-4.18, 6.25) * mm});
            skLineSegment(sketch, "E1105", {"start": v(-4.18, 6.25) * mm, "end": v(-4.18, 5.97) * mm});
            skLineSegment(sketch, "E1106", {"start": v(-4.18, 5.97) * mm, "end": v(-4.18, 1.51) * mm});
            skLineSegment(sketch, "E1107", {"start": v(-4.18, 1.51) * mm, "end": v(-3.96, 1.55) * mm});
            skLineSegment(sketch, "E1108", {"start": v(-3.96, 1.55) * mm, "end": v(-1.96, 2.04) * mm});
            skLineSegment(sketch, "E1109", {"start": v(-1.96, 2.04) * mm, "end": v(-1.8, 2.11) * mm});
            skLineSegment(sketch, "E1110", {"start": v(3.1, -16.9) * mm, "end": v(3.1, -17.02) * mm});
            skLineSegment(sketch, "E1111", {"start": v(3.1, -17.02) * mm, "end": v(3.17, -17.4) * mm});
            skLineSegment(sketch, "E1112", {"start": v(3.17, -17.4) * mm, "end": v(3.4, -17.81) * mm});
            skLineSegment(sketch, "E1113", {"start": v(3.4, -17.81) * mm, "end": v(3.77, -18.08) * mm});
            skLineSegment(sketch, "E1114", {"start": v(3.77, -18.08) * mm, "end": v(4.14, -18.18) * mm});
            skLineSegment(sketch, "E1115", {"start": v(4.14, -18.18) * mm, "end": v(4.27, -18.18) * mm});
            skLineSegment(sketch, "E1116", {"start": v(4.27, -18.18) * mm, "end": v(4.45, -18.18) * mm});
            skLineSegment(sketch, "E1117", {"start": v(4.45, -18.18) * mm, "end": v(5, -18.07) * mm});
            skLineSegment(sketch, "E1118", {"start": v(5, -18.07) * mm, "end": v(5.45, -17.84) * mm});
            skLineSegment(sketch, "E1119", {"start": v(5.45, -17.84) * mm, "end": v(5.5, -17.77) * mm});
            skLineSegment(sketch, "E1120", {"start": v(5.5, -17.77) * mm, "end": v(5.38, -18.6) * mm});
            skLineSegment(sketch, "E1121", {"start": v(5.38, -18.6) * mm, "end": v(5.33, -18.63) * mm});
            skLineSegment(sketch, "E1122", {"start": v(5.33, -18.63) * mm, "end": v(4.97, -18.73) * mm});
            skLineSegment(sketch, "E1123", {"start": v(4.97, -18.73) * mm, "end": v(4.46, -18.8) * mm});
            skLineSegment(sketch, "E1124", {"start": v(4.46, -18.8) * mm, "end": v(4.29, -18.8) * mm});
            skLineSegment(sketch, "E1125", {"start": v(4.29, -18.8) * mm, "end": v(4.08, -18.8) * mm});
            skLineSegment(sketch, "E1126", {"start": v(4.08, -18.8) * mm, "end": v(3.47, -18.67) * mm});
            skLineSegment(sketch, "E1127", {"start": v(3.47, -18.67) * mm, "end": v(2.83, -18.3) * mm});
            skLineSegment(sketch, "E1128", {"start": v(2.83, -18.3) * mm, "end": v(2.4, -17.7) * mm});
            skLineSegment(sketch, "E1129", {"start": v(2.4, -17.7) * mm, "end": v(2.26, -17.1) * mm});
            skLineSegment(sketch, "E1130", {"start": v(2.26, -17.1) * mm, "end": v(2.26, -16.9) * mm});
            skLineSegment(sketch, "E1131", {"start": v(2.26, -16.9) * mm, "end": v(2.26, -16.69) * mm});
            skLineSegment(sketch, "E1132", {"start": v(2.26, -16.69) * mm, "end": v(2.44, -16.05) * mm});
            skLineSegment(sketch, "E1133", {"start": v(2.44, -16.05) * mm, "end": v(2.8, -15.53) * mm});
            skLineSegment(sketch, "E1134", {"start": v(2.8, -15.53) * mm, "end": v(2.9, -15.45) * mm});
            skLineSegment(sketch, "E1135", {"start": v(2.9, -15.45) * mm, "end": v(2.99, -15.37) * mm});
            skLineSegment(sketch, "E1136", {"start": v(2.99, -15.37) * mm, "end": v(3.5, -15.1) * mm});
            skLineSegment(sketch, "E1137", {"start": v(3.5, -15.1) * mm, "end": v(4.1, -14.98) * mm});
            skLineSegment(sketch, "E1138", {"start": v(4.1, -14.98) * mm, "end": v(4.29, -14.98) * mm});
            skLineSegment(sketch, "E1139", {"start": v(4.29, -14.98) * mm, "end": v(4.46, -14.98) * mm});
            skLineSegment(sketch, "E1140", {"start": v(4.46, -14.98) * mm, "end": v(4.97, -15.05) * mm});
            skLineSegment(sketch, "E1141", {"start": v(4.97, -15.05) * mm, "end": v(5.33, -15.17) * mm});
            skLineSegment(sketch, "E1142", {"start": v(5.33, -15.17) * mm, "end": v(5.38, -15.2) * mm});
            skLineSegment(sketch, "E1143", {"start": v(5.38, -15.2) * mm, "end": v(5.38, -15.98) * mm});
            skLineSegment(sketch, "E1144", {"start": v(5.38, -15.98) * mm, "end": v(5.32, -15.92) * mm});
            skLineSegment(sketch, "E1145", {"start": v(5.32, -15.92) * mm, "end": v(4.93, -15.7) * mm});
            skLineSegment(sketch, "E1146", {"start": v(4.93, -15.7) * mm, "end": v(4.43, -15.6) * mm});
            skLineSegment(sketch, "E1147", {"start": v(4.43, -15.6) * mm, "end": v(4.27, -15.6) * mm});
            skLineSegment(sketch, "E1148", {"start": v(4.27, -15.6) * mm, "end": v(4.14, -15.6) * mm});
            skLineSegment(sketch, "E1149", {"start": v(4.14, -15.6) * mm, "end": v(3.77, -15.7) * mm});
            skLineSegment(sketch, "E1150", {"start": v(3.77, -15.7) * mm, "end": v(3.4, -15.97) * mm});
            skLineSegment(sketch, "E1151", {"start": v(3.4, -15.97) * mm, "end": v(3.17, -16.38) * mm});
            skLineSegment(sketch, "E1152", {"start": v(3.17, -16.38) * mm, "end": v(3.1, -16.77) * mm});
            skLineSegment(sketch, "E1153", {"start": v(3.1, -16.77) * mm, "end": v(3.1, -16.9) * mm});
            skLineSegment(sketch, "E1154", {"start": v(-6.57, -17.8) * mm, "end": v(-6.61, -17.7) * mm});
            skLineSegment(sketch, "E1155", {"start": v(-6.61, -17.7) * mm, "end": v(-6.83, -17.34) * mm});
            skLineSegment(sketch, "E1156", {"start": v(-6.83, -17.34) * mm, "end": v(-7.09, -17.1) * mm});
            skLineSegment(sketch, "E1157", {"start": v(-7.09, -17.1) * mm, "end": v(-7.15, -17.07) * mm});
            skLineSegment(sketch, "E1158", {"start": v(-7.15, -17.07) * mm, "end": v(-7.01, -17.04) * mm});
            skLineSegment(sketch, "E1159", {"start": v(-7.01, -17.04) * mm, "end": v(-6.52, -16.75) * mm});
            skLineSegment(sketch, "E1160", {"start": v(-6.52, -16.75) * mm, "end": v(-6.3, -16.27) * mm});
            skLineSegment(sketch, "E1161", {"start": v(-6.3, -16.27) * mm, "end": v(-6.3, -16.15) * mm});
            skLineSegment(sketch, "E1162", {"start": v(-6.3, -16.15) * mm, "end": v(-6.3, -16) * mm});
            skLineSegment(sketch, "E1163", {"start": v(-6.3, -16) * mm, "end": v(-6.45, -15.52) * mm});
            skLineSegment(sketch, "E1164", {"start": v(-6.45, -15.52) * mm, "end": v(-6.8, -15.19) * mm});
            skLineSegment(sketch, "E1165", {"start": v(-6.8, -15.19) * mm, "end": v(-6.9, -15.15) * mm});
            skLineSegment(sketch, "E1166", {"start": v(-6.9, -15.15) * mm, "end": v(-6.95, -15.13) * mm});
            skLineSegment(sketch, "E1167", {"start": v(-6.95, -15.13) * mm, "end": v(-7.67, -15.07) * mm});
            skLineSegment(sketch, "E1168", {"start": v(-7.67, -15.07) * mm, "end": v(-7.91, -15.07) * mm});
            skLineSegment(sketch, "E1169", {"start": v(-7.91, -15.07) * mm, "end": v(-9.77, -15.07) * mm});
            skLineSegment(sketch, "E1170", {"start": v(-9.77, -15.07) * mm, "end": v(-9.73, -15.1) * mm});
            skLineSegment(sketch, "E1171", {"start": v(-9.73, -15.1) * mm, "end": v(-9.57, -15.38) * mm});
            skLineSegment(sketch, "E1172", {"start": v(-9.57, -15.38) * mm, "end": v(-9.5, -15.75) * mm});
            skLineSegment(sketch, "E1173", {"start": v(-9.5, -15.75) * mm, "end": v(-9.5, -15.88) * mm});
            skLineSegment(sketch, "E1174", {"start": v(-9.5, -15.88) * mm, "end": v(-9.5, -17.92) * mm});
            skLineSegment(sketch, "E1175", {"start": v(-9.5, -17.92) * mm, "end": v(-9.5, -18.04) * mm});
            skLineSegment(sketch, "E1176", {"start": v(-9.5, -18.04) * mm, "end": v(-9.57, -18.4) * mm});
            skLineSegment(sketch, "E1177", {"start": v(-9.57, -18.4) * mm, "end": v(-9.73, -18.7) * mm});
            skLineSegment(sketch, "E1178", {"start": v(-9.73, -18.7) * mm, "end": v(-9.77, -18.73) * mm});
            skLineSegment(sketch, "E1179", {"start": v(-9.77, -18.73) * mm, "end": v(-8.45, -18.73) * mm});
            skLineSegment(sketch, "E1180", {"start": v(-8.45, -18.73) * mm, "end": v(-8.5, -18.7) * mm});
            skLineSegment(sketch, "E1181", {"start": v(-8.5, -18.7) * mm, "end": v(-8.65, -18.4) * mm});
            skLineSegment(sketch, "E1182", {"start": v(-8.65, -18.4) * mm, "end": v(-8.73, -18.04) * mm});
            skLineSegment(sketch, "E1183", {"start": v(-8.73, -18.04) * mm, "end": v(-8.73, -17.92) * mm});
            skLineSegment(sketch, "E1184", {"start": v(-8.73, -17.92) * mm, "end": v(-8.73, -17.26) * mm});
            skLineSegment(sketch, "E1185", {"start": v(-8.73, -17.26) * mm, "end": v(-8.17, -17.26) * mm});
            skLineSegment(sketch, "E1186", {"start": v(-8.17, -17.26) * mm, "end": v(-8.08, -17.26) * mm});
            skLineSegment(sketch, "E1187", {"start": v(-8.08, -17.26) * mm, "end": v(-7.8, -17.35) * mm});
            skLineSegment(sketch, "E1188", {"start": v(-7.8, -17.35) * mm, "end": v(-7.6, -17.55) * mm});
            skLineSegment(sketch, "E1189", {"start": v(-7.6, -17.55) * mm, "end": v(-7.57, -17.6) * mm});
            skLineSegment(sketch, "E1190", {"start": v(-7.57, -17.6) * mm, "end": v(-7.53, -17.68) * mm});
            skLineSegment(sketch, "E1191", {"start": v(-7.53, -17.68) * mm, "end": v(-7.06, -18.63) * mm});
            skLineSegment(sketch, "E1192", {"start": v(-7.06, -18.63) * mm, "end": v(-7, -18.71) * mm});
            skLineSegment(sketch, "E1193", {"start": v(-7, -18.71) * mm, "end": v(-5.9, -18.73) * mm});
            skLineSegment(sketch, "E1194", {"start": v(-5.9, -18.73) * mm, "end": v(-6, -18.67) * mm});
            skLineSegment(sketch, "E1195", {"start": v(-6, -18.67) * mm, "end": v(-6.3, -18.3) * mm});
            skLineSegment(sketch, "E1196", {"start": v(-6.3, -18.3) * mm, "end": v(-6.53, -17.89) * mm});
            skLineSegment(sketch, "E1197", {"start": v(-6.53, -17.89) * mm, "end": v(-6.57, -17.8) * mm});
            skLineSegment(sketch, "E1198", {"start": v(-7.1, -16.17) * mm, "end": v(-7.1, -16.27) * mm});
            skLineSegment(sketch, "E1199", {"start": v(-7.1, -16.27) * mm, "end": v(-7.31, -16.57) * mm});
            skLineSegment(sketch, "E1200", {"start": v(-7.31, -16.57) * mm, "end": v(-7.73, -16.69) * mm});
            skLineSegment(sketch, "E1201", {"start": v(-7.73, -16.69) * mm, "end": v(-7.87, -16.69) * mm});
            skLineSegment(sketch, "E1202", {"start": v(-7.87, -16.69) * mm, "end": v(-8.73, -16.69) * mm});
            skLineSegment(sketch, "E1203", {"start": v(-8.73, -16.69) * mm, "end": v(-8.73, -15.66) * mm});
            skLineSegment(sketch, "E1204", {"start": v(-8.73, -15.66) * mm, "end": v(-7.87, -15.66) * mm});
            skLineSegment(sketch, "E1205", {"start": v(-7.87, -15.66) * mm, "end": v(-7.73, -15.66) * mm});
            skLineSegment(sketch, "E1206", {"start": v(-7.73, -15.66) * mm, "end": v(-7.31, -15.77) * mm});
            skLineSegment(sketch, "E1207", {"start": v(-7.31, -15.77) * mm, "end": v(-7.1, -16.07) * mm});
            skLineSegment(sketch, "E1208", {"start": v(-7.1, -16.07) * mm, "end": v(-7.1, -16.17) * mm});
            skLineSegment(sketch, "E1209", {"start": v(-4.5, -17.86) * mm, "end": v(-4.56, -17.81) * mm});
            skLineSegment(sketch, "E1210", {"start": v(-4.56, -17.81) * mm, "end": v(-4.74, -17.48) * mm});
            skLineSegment(sketch, "E1211", {"start": v(-4.74, -17.48) * mm, "end": v(-4.82, -17.04) * mm});
            skLineSegment(sketch, "E1212", {"start": v(-4.82, -17.04) * mm, "end": v(-4.82, -16.9) * mm});
            skLineSegment(sketch, "E1213", {"start": v(-4.82, -16.9) * mm, "end": v(-4.82, -16.75) * mm});
            skLineSegment(sketch, "E1214", {"start": v(-4.82, -16.75) * mm, "end": v(-4.74, -16.32) * mm});
            skLineSegment(sketch, "E1215", {"start": v(-4.74, -16.32) * mm, "end": v(-4.56, -15.97) * mm});
            skLineSegment(sketch, "E1216", {"start": v(-4.56, -15.97) * mm, "end": v(-4.5, -15.92) * mm});
            skLineSegment(sketch, "E1217", {"start": v(-4.5, -15.92) * mm, "end": v(-4.45, -15.87) * mm});
            skLineSegment(sketch, "E1218", {"start": v(-4.45, -15.87) * mm, "end": v(-3.9, -15.62) * mm});
            skLineSegment(sketch, "E1219", {"start": v(-3.9, -15.62) * mm, "end": v(-3.71, -15.62) * mm});
            skLineSegment(sketch, "E1220", {"start": v(-3.71, -15.62) * mm, "end": v(-3.52, -15.62) * mm});
            skLineSegment(sketch, "E1221", {"start": v(-3.52, -15.62) * mm, "end": v(-3, -15.87) * mm});
            skLineSegment(sketch, "E1222", {"start": v(-3, -15.87) * mm, "end": v(-2.94, -15.92) * mm});
            skLineSegment(sketch, "E1223", {"start": v(-2.94, -15.92) * mm, "end": v(-2.9, -15.97) * mm});
            skLineSegment(sketch, "E1224", {"start": v(-2.9, -15.97) * mm, "end": v(-2.62, -16.67) * mm});
            skLineSegment(sketch, "E1225", {"start": v(-2.62, -16.67) * mm, "end": v(-2.62, -16.9) * mm});
            skLineSegment(sketch, "E1226", {"start": v(-2.62, -16.9) * mm, "end": v(-2.62, -17.14) * mm});
            skLineSegment(sketch, "E1227", {"start": v(-2.62, -17.14) * mm, "end": v(-2.9, -17.81) * mm});
            skLineSegment(sketch, "E1228", {"start": v(-2.9, -17.81) * mm, "end": v(-2.94, -17.86) * mm});
            skLineSegment(sketch, "E1229", {"start": v(-2.94, -17.86) * mm, "end": v(-3, -17.9) * mm});
            skLineSegment(sketch, "E1230", {"start": v(-3, -17.9) * mm, "end": v(-3.53, -18.18) * mm});
            skLineSegment(sketch, "E1231", {"start": v(-3.53, -18.18) * mm, "end": v(-3.71, -18.18) * mm});
            skLineSegment(sketch, "E1232", {"start": v(-3.71, -18.18) * mm, "end": v(-3.91, -18.18) * mm});
            skLineSegment(sketch, "E1233", {"start": v(-3.91, -18.18) * mm, "end": v(-4.45, -17.9) * mm});
            skLineSegment(sketch, "E1234", {"start": v(-4.45, -17.9) * mm, "end": v(-4.5, -17.86) * mm});
            skLineSegment(sketch, "E1235", {"start": v(-3.73, -18.82) * mm, "end": v(-3.56, -18.82) * mm});
            skLineSegment(sketch, "E1236", {"start": v(-3.56, -18.82) * mm, "end": v(-3.03, -18.7) * mm});
            skLineSegment(sketch, "E1237", {"start": v(-3.03, -18.7) * mm, "end": v(-2.55, -18.46) * mm});
            skLineSegment(sketch, "E1238", {"start": v(-2.55, -18.46) * mm, "end": v(-2.47, -18.4) * mm});
            skLineSegment(sketch, "E1239", {"start": v(-2.47, -18.4) * mm, "end": v(-2.38, -18.31) * mm});
            skLineSegment(sketch, "E1240", {"start": v(-2.38, -18.31) * mm, "end": v(-2, -17.78) * mm});
            skLineSegment(sketch, "E1241", {"start": v(-2, -17.78) * mm, "end": v(-1.81, -17.12) * mm});
            skLineSegment(sketch, "E1242", {"start": v(-1.81, -17.12) * mm, "end": v(-1.81, -16.9) * mm});
            skLineSegment(sketch, "E1243", {"start": v(-1.81, -16.9) * mm, "end": v(-1.81, -16.68) * mm});
            skLineSegment(sketch, "E1244", {"start": v(-1.81, -16.68) * mm, "end": v(-2, -16.01) * mm});
            skLineSegment(sketch, "E1245", {"start": v(-2, -16.01) * mm, "end": v(-2.38, -15.47) * mm});
            skLineSegment(sketch, "E1246", {"start": v(-2.38, -15.47) * mm, "end": v(-2.47, -15.38) * mm});
            skLineSegment(sketch, "E1247", {"start": v(-2.47, -15.38) * mm, "end": v(-2.55, -15.32) * mm});
            skLineSegment(sketch, "E1248", {"start": v(-2.55, -15.32) * mm, "end": v(-3.03, -15.08) * mm});
            skLineSegment(sketch, "E1249", {"start": v(-3.03, -15.08) * mm, "end": v(-3.56, -14.98) * mm});
            skLineSegment(sketch, "E1250", {"start": v(-3.56, -14.98) * mm, "end": v(-3.73, -14.98) * mm});
            skLineSegment(sketch, "E1251", {"start": v(-3.73, -14.98) * mm, "end": v(-3.9, -14.98) * mm});
            skLineSegment(sketch, "E1252", {"start": v(-3.9, -14.98) * mm, "end": v(-4.42, -15.08) * mm});
            skLineSegment(sketch, "E1253", {"start": v(-4.42, -15.08) * mm, "end": v(-4.9, -15.32) * mm});
            skLineSegment(sketch, "E1254", {"start": v(-4.9, -15.32) * mm, "end": v(-4.97, -15.38) * mm});
            skLineSegment(sketch, "E1255", {"start": v(-4.97, -15.38) * mm, "end": v(-5.07, -15.47) * mm});
            skLineSegment(sketch, "E1256", {"start": v(-5.07, -15.47) * mm, "end": v(-5.45, -16.01) * mm});
            skLineSegment(sketch, "E1257", {"start": v(-5.45, -16.01) * mm, "end": v(-5.63, -16.68) * mm});
            skLineSegment(sketch, "E1258", {"start": v(-5.63, -16.68) * mm, "end": v(-5.63, -16.9) * mm});
            skLineSegment(sketch, "E1259", {"start": v(-5.63, -16.9) * mm, "end": v(-5.63, -17.12) * mm});
            skLineSegment(sketch, "E1260", {"start": v(-5.63, -17.12) * mm, "end": v(-5.45, -17.78) * mm});
            skLineSegment(sketch, "E1261", {"start": v(-5.45, -17.78) * mm, "end": v(-5.07, -18.31) * mm});
            skLineSegment(sketch, "E1262", {"start": v(-5.07, -18.31) * mm, "end": v(-4.97, -18.4) * mm});
            skLineSegment(sketch, "E1263", {"start": v(-4.97, -18.4) * mm, "end": v(-4.9, -18.46) * mm});
            skLineSegment(sketch, "E1264", {"start": v(-4.9, -18.46) * mm, "end": v(-4.42, -18.7) * mm});
            skLineSegment(sketch, "E1265", {"start": v(-4.42, -18.7) * mm, "end": v(-3.9, -18.82) * mm});
            skLineSegment(sketch, "E1266", {"start": v(-3.9, -18.82) * mm, "end": v(-3.73, -18.82) * mm});
            skLineSegment(sketch, "E1267", {"start": v(1.05, -15.07) * mm, "end": v(1.07, -15.08) * mm});
            skLineSegment(sketch, "E1268", {"start": v(1.07, -15.08) * mm, "end": v(1.16, -15.26) * mm});
            skLineSegment(sketch, "E1269", {"start": v(1.16, -15.26) * mm, "end": v(1.15, -15.28) * mm});
            skLineSegment(sketch, "E1270", {"start": v(1.15, -15.28) * mm, "end": v(1.05, -15.59) * mm});
            skLineSegment(sketch, "E1271", {"start": v(1.05, -15.59) * mm, "end": v(1.03, -15.62) * mm});
            skLineSegment(sketch, "E1272", {"start": v(1.03, -15.62) * mm, "end": v(0.3, -16.67) * mm});
            skLineSegment(sketch, "E1273", {"start": v(0.3, -16.67) * mm, "end": v(-0.43, -15.6) * mm});
            skLineSegment(sketch, "E1274", {"start": v(-0.43, -15.6) * mm, "end": v(-0.45, -15.57) * mm});
            skLineSegment(sketch, "E1275", {"start": v(-0.45, -15.57) * mm, "end": v(-0.58, -15.26) * mm});
            skLineSegment(sketch, "E1276", {"start": v(-0.58, -15.26) * mm, "end": v(-0.58, -15.24) * mm});
            skLineSegment(sketch, "E1277", {"start": v(-0.58, -15.24) * mm, "end": v(-0.57, -15.22) * mm});
            skLineSegment(sketch, "E1278", {"start": v(-0.57, -15.22) * mm, "end": v(-0.47, -15.07) * mm});
            skLineSegment(sketch, "E1279", {"start": v(-0.47, -15.07) * mm, "end": v(-0.45, -15.07) * mm});
            skLineSegment(sketch, "E1280", {"start": v(-0.45, -15.07) * mm, "end": v(-1.92, -15.07) * mm});
            skLineSegment(sketch, "E1281", {"start": v(-1.92, -15.07) * mm, "end": v(-1.86, -15.1) * mm});
            skLineSegment(sketch, "E1282", {"start": v(-1.86, -15.1) * mm, "end": v(-1.4, -15.57) * mm});
            skLineSegment(sketch, "E1283", {"start": v(-1.4, -15.57) * mm, "end": v(-1.34, -15.64) * mm});
            skLineSegment(sketch, "E1284", {"start": v(-1.34, -15.64) * mm, "end": v(-0.15, -17.33) * mm});
            skLineSegment(sketch, "E1285", {"start": v(-0.15, -17.33) * mm, "end": v(-0.15, -17.92) * mm});
            skLineSegment(sketch, "E1286", {"start": v(-0.15, -17.92) * mm, "end": v(-0.15, -18.04) * mm});
            skLineSegment(sketch, "E1287", {"start": v(-0.15, -18.04) * mm, "end": v(-0.22, -18.4) * mm});
            skLineSegment(sketch, "E1288", {"start": v(-0.22, -18.4) * mm, "end": v(-0.38, -18.69) * mm});
            skLineSegment(sketch, "E1289", {"start": v(-0.38, -18.69) * mm, "end": v(-0.43, -18.71) * mm});
            skLineSegment(sketch, "E1290", {"start": v(-0.43, -18.71) * mm, "end": v(0.9, -18.71) * mm});
            skLineSegment(sketch, "E1291", {"start": v(0.9, -18.71) * mm, "end": v(0.85, -18.69) * mm});
            skLineSegment(sketch, "E1292", {"start": v(0.85, -18.69) * mm, "end": v(0.7, -18.4) * mm});
            skLineSegment(sketch, "E1293", {"start": v(0.7, -18.4) * mm, "end": v(0.62, -18.04) * mm});
            skLineSegment(sketch, "E1294", {"start": v(0.62, -18.04) * mm, "end": v(0.62, -17.92) * mm});
            skLineSegment(sketch, "E1295", {"start": v(0.62, -17.92) * mm, "end": v(0.62, -17.33) * mm});
            skLineSegment(sketch, "E1296", {"start": v(0.62, -17.33) * mm, "end": v(1.7, -15.8) * mm});
            skLineSegment(sketch, "E1297", {"start": v(1.7, -15.8) * mm, "end": v(1.75, -15.74) * mm});
            skLineSegment(sketch, "E1298", {"start": v(1.75, -15.74) * mm, "end": v(2, -15.4) * mm});
            skLineSegment(sketch, "E1299", {"start": v(2, -15.4) * mm, "end": v(2.3, -15.1) * mm});
            skLineSegment(sketch, "E1300", {"start": v(2.3, -15.1) * mm, "end": v(2.37, -15.07) * mm});
            skLineSegment(sketch, "E1301", {"start": v(2.37, -15.07) * mm, "end": v(1.05, -15.07) * mm});
            skLineSegment(sketch, "E1302", {"start": v(8.13, -18.14) * mm, "end": v(7.2, -18.14) * mm});
            skLineSegment(sketch, "E1303", {"start": v(7.2, -18.14) * mm, "end": v(7.2, -17.14) * mm});
            skLineSegment(sketch, "E1304", {"start": v(7.2, -17.14) * mm, "end": v(8.6, -17.14) * mm});
            skLineSegment(sketch, "E1305", {"start": v(8.6, -17.14) * mm, "end": v(8.69, -16.58) * mm});
            skLineSegment(sketch, "E1306", {"start": v(8.69, -16.58) * mm, "end": v(7.2, -16.58) * mm});
            skLineSegment(sketch, "E1307", {"start": v(7.2, -16.58) * mm, "end": v(7.2, -15.66) * mm});
            skLineSegment(sketch, "E1308", {"start": v(7.2, -15.66) * mm, "end": v(8.02, -15.66) * mm});
            skLineSegment(sketch, "E1309", {"start": v(8.02, -15.66) * mm, "end": v(8.18, -15.66) * mm});
            skLineSegment(sketch, "E1310", {"start": v(8.18, -15.66) * mm, "end": v(8.65, -15.7) * mm});
            skLineSegment(sketch, "E1311", {"start": v(8.65, -15.7) * mm, "end": v(9.02, -15.83) * mm});
            skLineSegment(sketch, "E1312", {"start": v(9.02, -15.83) * mm, "end": v(9.07, -15.88) * mm});
            skLineSegment(sketch, "E1313", {"start": v(9.07, -15.88) * mm, "end": v(9.07, -15.07) * mm});
            skLineSegment(sketch, "E1314", {"start": v(9.07, -15.07) * mm, "end": v(6.15, -15.07) * mm});
            skLineSegment(sketch, "E1315", {"start": v(6.15, -15.07) * mm, "end": v(6.19, -15.1) * mm});
            skLineSegment(sketch, "E1316", {"start": v(6.19, -15.1) * mm, "end": v(6.35, -15.4) * mm});
            skLineSegment(sketch, "E1317", {"start": v(6.35, -15.4) * mm, "end": v(6.42, -15.76) * mm});
            skLineSegment(sketch, "E1318", {"start": v(6.42, -15.76) * mm, "end": v(6.42, -15.88) * mm});
            skLineSegment(sketch, "E1319", {"start": v(6.42, -15.88) * mm, "end": v(6.42, -17.92) * mm});
            skLineSegment(sketch, "E1320", {"start": v(6.42, -17.92) * mm, "end": v(6.42, -18.04) * mm});
            skLineSegment(sketch, "E1321", {"start": v(6.42, -18.04) * mm, "end": v(6.35, -18.4) * mm});
            skLineSegment(sketch, "E1322", {"start": v(6.35, -18.4) * mm, "end": v(6.19, -18.7) * mm});
            skLineSegment(sketch, "E1323", {"start": v(6.19, -18.7) * mm, "end": v(6.15, -18.73) * mm});
            skLineSegment(sketch, "E1324", {"start": v(6.15, -18.73) * mm, "end": v(9.1, -18.73) * mm});
            skLineSegment(sketch, "E1325", {"start": v(9.1, -18.73) * mm, "end": v(9.22, -17.84) * mm});
            skLineSegment(sketch, "E1326", {"start": v(9.22, -17.84) * mm, "end": v(9.16, -17.9) * mm});
            skLineSegment(sketch, "E1327", {"start": v(9.16, -17.9) * mm, "end": v(8.77, -18.1) * mm});
            skLineSegment(sketch, "E1328", {"start": v(8.77, -18.1) * mm, "end": v(8.29, -18.14) * mm});
            skLineSegment(sketch, "E1329", {"start": v(8.29, -18.14) * mm, "end": v(8.13, -18.14) * mm});
            skSolve(sketch);
        }
        {
            var Q0;
            Q0 = qSketchRegion(id + "F4", true);
            extrude(context, id + "F5", {"entities" : qUnion([Q0]), "operationType" : NewBodyOperationType.REMOVE, "oppositeDirection" : true, "depth" : 1.27 * mm, "offsetDistance" : 25.4 * mm});
        }
    });
